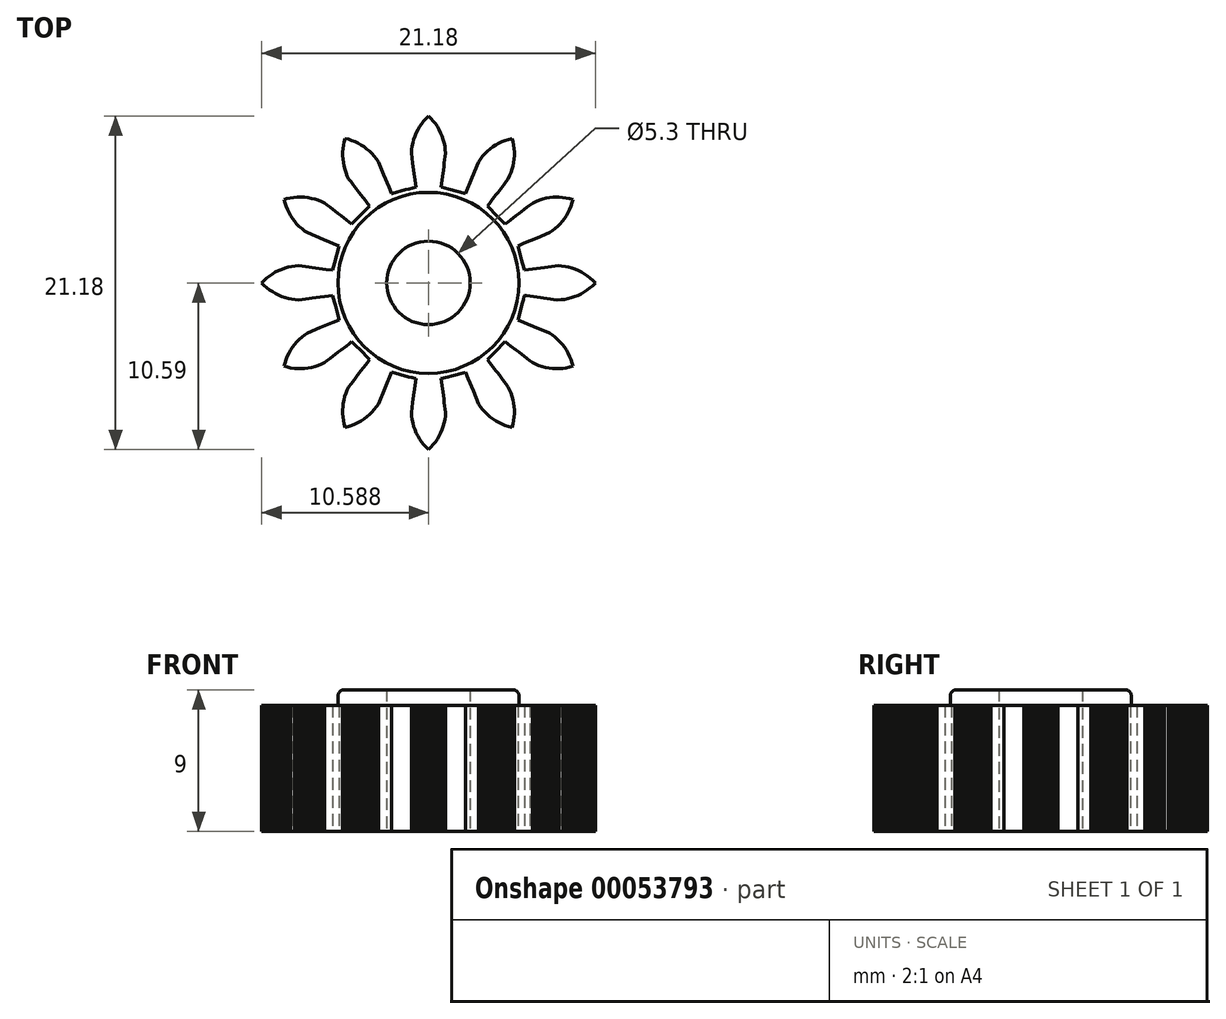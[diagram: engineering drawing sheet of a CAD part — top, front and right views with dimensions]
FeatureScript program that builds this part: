
annotation { "Feature Type Name" : "Feature", "Feature Type Description" : "" }
export const myFeature = defineFeature(function(context is Context, id is Id, definition is map)
    precondition{}
    {
        {
            var Q0;
            Q0=qCreatedBy(makeId("Top.planeOp"),FACE);
            var sketch = newSketch(context, id + "F0", { "sketchPlane" : qUnion([Q0])});
            skLineSegment(sketch, "E0", {"start": v(4.76, -0.8) * mm, "end": v(4.9, -0.82) * mm});
            skLineSegment(sketch, "E1", {"start": v(4.9, -0.82) * mm, "end": v(5.12, -0.85) * mm});
            skLineSegment(sketch, "E2", {"start": v(5.12, -0.85) * mm, "end": v(5.33, -0.88) * mm});
            skLineSegment(sketch, "E3", {"start": v(5.33, -0.88) * mm, "end": v(5.55, -0.9) * mm});
            skLineSegment(sketch, "E4", {"start": v(5.55, -0.9) * mm, "end": v(5.76, -0.93) * mm});
            skLineSegment(sketch, "E5", {"start": v(5.76, -0.93) * mm, "end": v(5.98, -0.96) * mm});
            skLineSegment(sketch, "E6", {"start": v(5.98, -0.96) * mm, "end": v(6.2, -1) * mm});
            skLineSegment(sketch, "E7", {"start": v(6.2, -1) * mm, "end": v(6.41, -1.02) * mm});
            skLineSegment(sketch, "E8", {"start": v(6.41, -1.02) * mm, "end": v(6.63, -1.05) * mm});
            skLineSegment(sketch, "E9", {"start": v(6.63, -1.05) * mm, "end": v(6.84, -1.08) * mm});
            skLineSegment(sketch, "E10", {"start": v(6.84, -1.08) * mm, "end": v(7.07, -1.07) * mm});
            skLineSegment(sketch, "E11", {"start": v(7.07, -1.07) * mm, "end": v(7.3, -1.05) * mm});
            skLineSegment(sketch, "E12", {"start": v(7.3, -1.05) * mm, "end": v(7.53, -1) * mm});
            skLineSegment(sketch, "E13", {"start": v(7.53, -1) * mm, "end": v(7.75, -0.95) * mm});
            skLineSegment(sketch, "E14", {"start": v(7.75, -0.95) * mm, "end": v(7.95, -0.88) * mm});
            skLineSegment(sketch, "E15", {"start": v(7.95, -0.88) * mm, "end": v(8.16, -0.8) * mm});
            skLineSegment(sketch, "E16", {"start": v(8.16, -0.8) * mm, "end": v(8.36, -0.7) * mm});
            skLineSegment(sketch, "E17", {"start": v(8.36, -0.7) * mm, "end": v(8.55, -0.59) * mm});
            skLineSegment(sketch, "E18", {"start": v(8.55, -0.59) * mm, "end": v(8.73, -0.47) * mm});
            skLineSegment(sketch, "E19", {"start": v(8.73, -0.47) * mm, "end": v(8.9, -0.33) * mm});
            skLineSegment(sketch, "E20", {"start": v(8.9, -0.33) * mm, "end": v(9.07, -0.19) * mm});
            skLineSegment(sketch, "E21", {"start": v(9.07, -0.19) * mm, "end": v(9.23, -0.03) * mm});
            skLineSegment(sketch, "E22", {"start": v(9.23, -0.03) * mm, "end": v(9.26, 0) * mm});
            skLineSegment(sketch, "E23", {"start": v(9.26, 0) * mm, "end": v(9.1, 0.16) * mm});
            skLineSegment(sketch, "E24", {"start": v(9.1, 0.16) * mm, "end": v(8.94, 0.3) * mm});
            skLineSegment(sketch, "E25", {"start": v(8.94, 0.3) * mm, "end": v(8.76, 0.44) * mm});
            skLineSegment(sketch, "E26", {"start": v(8.76, 0.44) * mm, "end": v(8.58, 0.57) * mm});
            skLineSegment(sketch, "E27", {"start": v(8.58, 0.57) * mm, "end": v(8.39, 0.68) * mm});
            skLineSegment(sketch, "E28", {"start": v(8.39, 0.68) * mm, "end": v(8.2, 0.78) * mm});
            skLineSegment(sketch, "E29", {"start": v(8.2, 0.78) * mm, "end": v(7.99, 0.86) * mm});
            skLineSegment(sketch, "E30", {"start": v(7.99, 0.86) * mm, "end": v(7.78, 0.94) * mm});
            skLineSegment(sketch, "E31", {"start": v(7.78, 0.94) * mm, "end": v(7.57, 1) * mm});
            skLineSegment(sketch, "E32", {"start": v(7.57, 1) * mm, "end": v(7.36, 1.04) * mm});
            skLineSegment(sketch, "E33", {"start": v(7.36, 1.04) * mm, "end": v(7.13, 1.07) * mm});
            skLineSegment(sketch, "E34", {"start": v(7.13, 1.07) * mm, "end": v(6.92, 1.09) * mm});
            skLineSegment(sketch, "E35", {"start": v(6.92, 1.09) * mm, "end": v(6.7, 1.06) * mm});
            skLineSegment(sketch, "E36", {"start": v(6.7, 1.06) * mm, "end": v(6.48, 1.03) * mm});
            skLineSegment(sketch, "E37", {"start": v(6.48, 1.03) * mm, "end": v(6.27, 1) * mm});
            skLineSegment(sketch, "E38", {"start": v(6.27, 1) * mm, "end": v(6.05, 0.97) * mm});
            skLineSegment(sketch, "E39", {"start": v(6.05, 0.97) * mm, "end": v(5.84, 0.94) * mm});
            skLineSegment(sketch, "E40", {"start": v(5.84, 0.94) * mm, "end": v(5.62, 0.92) * mm});
            skLineSegment(sketch, "E41", {"start": v(5.62, 0.92) * mm, "end": v(5.4, 0.89) * mm});
            skLineSegment(sketch, "E42", {"start": v(5.4, 0.89) * mm, "end": v(5.19, 0.86) * mm});
            skLineSegment(sketch, "E43", {"start": v(5.19, 0.86) * mm, "end": v(4.97, 0.83) * mm});
            skLineSegment(sketch, "E44", {"start": v(4.97, 0.83) * mm, "end": v(4.76, 0.8) * mm});
            skLineSegment(sketch, "E45", {"start": v(4.76, 0.8) * mm, "end": v(4.7, 1.02) * mm});
            skLineSegment(sketch, "E46", {"start": v(4.7, 1.02) * mm, "end": v(4.64, 1.24) * mm});
            skLineSegment(sketch, "E47", {"start": v(4.64, 1.24) * mm, "end": v(4.58, 1.45) * mm});
            skLineSegment(sketch, "E48", {"start": v(4.58, 1.45) * mm, "end": v(4.52, 1.67) * mm});
            skLineSegment(sketch, "E49", {"start": v(4.52, 1.67) * mm, "end": v(4.47, 1.89) * mm});
            skLineSegment(sketch, "E50", {"start": v(4.47, 1.89) * mm, "end": v(4.4, 2.1) * mm});
            skLineSegment(sketch, "E51", {"start": v(4.4, 2.1) * mm, "end": v(4.35, 2.32) * mm});
            skLineSegment(sketch, "E52", {"start": v(4.35, 2.32) * mm, "end": v(4.34, 2.35) * mm});
            skLineSegment(sketch, "E53", {"start": v(4.34, 2.35) * mm, "end": v(4.54, 2.43) * mm});
            skLineSegment(sketch, "E54", {"start": v(4.54, 2.43) * mm, "end": v(4.74, 2.52) * mm});
            skLineSegment(sketch, "E55", {"start": v(4.74, 2.52) * mm, "end": v(4.95, 2.6) * mm});
            skLineSegment(sketch, "E56", {"start": v(4.95, 2.6) * mm, "end": v(5.15, 2.68) * mm});
            skLineSegment(sketch, "E57", {"start": v(5.15, 2.68) * mm, "end": v(5.35, 2.77) * mm});
            skLineSegment(sketch, "E58", {"start": v(5.35, 2.77) * mm, "end": v(5.55, 2.85) * mm});
            skLineSegment(sketch, "E59", {"start": v(5.55, 2.85) * mm, "end": v(5.75, 2.93) * mm});
            skLineSegment(sketch, "E60", {"start": v(5.75, 2.93) * mm, "end": v(5.95, 3.02) * mm});
            skLineSegment(sketch, "E61", {"start": v(5.95, 3.02) * mm, "end": v(6.15, 3.1) * mm});
            skLineSegment(sketch, "E62", {"start": v(6.15, 3.1) * mm, "end": v(6.35, 3.18) * mm});
            skLineSegment(sketch, "E63", {"start": v(6.35, 3.18) * mm, "end": v(6.54, 3.31) * mm});
            skLineSegment(sketch, "E64", {"start": v(6.54, 3.31) * mm, "end": v(6.71, 3.44) * mm});
            skLineSegment(sketch, "E65", {"start": v(6.71, 3.44) * mm, "end": v(6.88, 3.6) * mm});
            skLineSegment(sketch, "E66", {"start": v(6.88, 3.6) * mm, "end": v(7.03, 3.75) * mm});
            skLineSegment(sketch, "E67", {"start": v(7.03, 3.75) * mm, "end": v(7.18, 3.92) * mm});
            skLineSegment(sketch, "E68", {"start": v(7.18, 3.92) * mm, "end": v(7.3, 4.1) * mm});
            skLineSegment(sketch, "E69", {"start": v(7.3, 4.1) * mm, "end": v(7.43, 4.28) * mm});
            skLineSegment(sketch, "E70", {"start": v(7.43, 4.28) * mm, "end": v(7.54, 4.47) * mm});
            skLineSegment(sketch, "E71", {"start": v(7.54, 4.47) * mm, "end": v(7.64, 4.67) * mm});
            skLineSegment(sketch, "E72", {"start": v(7.64, 4.67) * mm, "end": v(7.72, 4.87) * mm});
            skLineSegment(sketch, "E73", {"start": v(7.72, 4.87) * mm, "end": v(7.79, 5.09) * mm});
            skLineSegment(sketch, "E74", {"start": v(7.79, 5.09) * mm, "end": v(7.84, 5.3) * mm});
            skLineSegment(sketch, "E75", {"start": v(7.84, 5.3) * mm, "end": v(7.62, 5.36) * mm});
            skLineSegment(sketch, "E76", {"start": v(7.62, 5.36) * mm, "end": v(7.41, 5.4) * mm});
            skLineSegment(sketch, "E77", {"start": v(7.41, 5.4) * mm, "end": v(7.19, 5.43) * mm});
            skLineSegment(sketch, "E78", {"start": v(7.19, 5.43) * mm, "end": v(6.97, 5.45) * mm});
            skLineSegment(sketch, "E79", {"start": v(6.97, 5.45) * mm, "end": v(6.8, 5.45) * mm});
            skLineSegment(sketch, "E80", {"start": v(6.8, 5.45) * mm, "end": v(6.57, 5.44) * mm});
            skLineSegment(sketch, "E81", {"start": v(6.57, 5.44) * mm, "end": v(6.36, 5.42) * mm});
            skLineSegment(sketch, "E82", {"start": v(6.36, 5.42) * mm, "end": v(6.13, 5.38) * mm});
            skLineSegment(sketch, "E83", {"start": v(6.13, 5.38) * mm, "end": v(5.92, 5.33) * mm});
            skLineSegment(sketch, "E84", {"start": v(5.92, 5.33) * mm, "end": v(5.7, 5.26) * mm});
            skLineSegment(sketch, "E85", {"start": v(5.7, 5.26) * mm, "end": v(5.5, 5.18) * mm});
            skLineSegment(sketch, "E86", {"start": v(5.5, 5.18) * mm, "end": v(5.3, 5.08) * mm});
            skLineSegment(sketch, "E87", {"start": v(5.3, 5.08) * mm, "end": v(5.12, 4.95) * mm});
            skLineSegment(sketch, "E88", {"start": v(5.12, 4.95) * mm, "end": v(4.94, 4.81) * mm});
            skLineSegment(sketch, "E89", {"start": v(4.94, 4.81) * mm, "end": v(4.75, 4.67) * mm});
            skLineSegment(sketch, "E90", {"start": v(4.75, 4.67) * mm, "end": v(4.58, 4.53) * mm});
            skLineSegment(sketch, "E91", {"start": v(4.58, 4.53) * mm, "end": v(4.4, 4.4) * mm});
            skLineSegment(sketch, "E92", {"start": v(4.4, 4.4) * mm, "end": v(4.23, 4.27) * mm});
            skLineSegment(sketch, "E93", {"start": v(4.23, 4.27) * mm, "end": v(4.06, 4.14) * mm});
            skLineSegment(sketch, "E94", {"start": v(4.06, 4.14) * mm, "end": v(3.89, 4) * mm});
            skLineSegment(sketch, "E95", {"start": v(3.89, 4) * mm, "end": v(3.71, 3.87) * mm});
            skLineSegment(sketch, "E96", {"start": v(3.71, 3.87) * mm, "end": v(3.54, 3.74) * mm});
            skLineSegment(sketch, "E97", {"start": v(3.54, 3.74) * mm, "end": v(3.38, 3.9) * mm});
            skLineSegment(sketch, "E98", {"start": v(3.38, 3.9) * mm, "end": v(3.22, 4.06) * mm});
            skLineSegment(sketch, "E99", {"start": v(3.22, 4.06) * mm, "end": v(3.06, 4.22) * mm});
            skLineSegment(sketch, "E100", {"start": v(3.06, 4.22) * mm, "end": v(2.9, 4.38) * mm});
            skLineSegment(sketch, "E101", {"start": v(2.9, 4.38) * mm, "end": v(2.74, 4.53) * mm});
            skLineSegment(sketch, "E102", {"start": v(2.74, 4.53) * mm, "end": v(2.58, 4.7) * mm});
            skLineSegment(sketch, "E103", {"start": v(2.58, 4.7) * mm, "end": v(2.43, 4.85) * mm});
            skLineSegment(sketch, "E104", {"start": v(2.43, 4.85) * mm, "end": v(2.4, 4.87) * mm});
            skLineSegment(sketch, "E105", {"start": v(2.4, 4.87) * mm, "end": v(2.54, 5.04) * mm});
            skLineSegment(sketch, "E106", {"start": v(2.54, 5.04) * mm, "end": v(2.67, 5.22) * mm});
            skLineSegment(sketch, "E107", {"start": v(2.67, 5.22) * mm, "end": v(2.8, 5.4) * mm});
            skLineSegment(sketch, "E108", {"start": v(2.8, 5.4) * mm, "end": v(2.94, 5.56) * mm});
            skLineSegment(sketch, "E109", {"start": v(2.94, 5.56) * mm, "end": v(3.07, 5.74) * mm});
            skLineSegment(sketch, "E110", {"start": v(3.07, 5.74) * mm, "end": v(3.2, 5.9) * mm});
            skLineSegment(sketch, "E111", {"start": v(3.2, 5.9) * mm, "end": v(3.33, 6.08) * mm});
            skLineSegment(sketch, "E112", {"start": v(3.33, 6.08) * mm, "end": v(3.47, 6.25) * mm});
            skLineSegment(sketch, "E113", {"start": v(3.47, 6.25) * mm, "end": v(3.6, 6.43) * mm});
            skLineSegment(sketch, "E114", {"start": v(3.6, 6.43) * mm, "end": v(3.73, 6.6) * mm});
            skLineSegment(sketch, "E115", {"start": v(3.73, 6.6) * mm, "end": v(3.83, 6.8) * mm});
            skLineSegment(sketch, "E116", {"start": v(3.83, 6.8) * mm, "end": v(3.91, 7) * mm});
            skLineSegment(sketch, "E117", {"start": v(3.91, 7) * mm, "end": v(3.98, 7.22) * mm});
            skLineSegment(sketch, "E118", {"start": v(3.98, 7.22) * mm, "end": v(4.04, 7.43) * mm});
            skLineSegment(sketch, "E119", {"start": v(4.04, 7.43) * mm, "end": v(4.08, 7.65) * mm});
            skLineSegment(sketch, "E120", {"start": v(4.08, 7.65) * mm, "end": v(4.1, 7.86) * mm});
            skLineSegment(sketch, "E121", {"start": v(4.1, 7.86) * mm, "end": v(4.12, 8.09) * mm});
            skLineSegment(sketch, "E122", {"start": v(4.12, 8.09) * mm, "end": v(4.12, 8.3) * mm});
            skLineSegment(sketch, "E123", {"start": v(4.12, 8.3) * mm, "end": v(4.1, 8.53) * mm});
            skLineSegment(sketch, "E124", {"start": v(4.1, 8.53) * mm, "end": v(4.07, 8.74) * mm});
            skLineSegment(sketch, "E125", {"start": v(4.07, 8.74) * mm, "end": v(4.02, 8.96) * mm});
            skLineSegment(sketch, "E126", {"start": v(4.02, 8.96) * mm, "end": v(3.96, 9.17) * mm});
            skLineSegment(sketch, "E127", {"start": v(3.96, 9.17) * mm, "end": v(3.75, 9.12) * mm});
            skLineSegment(sketch, "E128", {"start": v(3.75, 9.12) * mm, "end": v(3.54, 9.05) * mm});
            skLineSegment(sketch, "E129", {"start": v(3.54, 9.05) * mm, "end": v(3.33, 8.96) * mm});
            skLineSegment(sketch, "E130", {"start": v(3.33, 8.96) * mm, "end": v(3.14, 8.87) * mm});
            skLineSegment(sketch, "E131", {"start": v(3.14, 8.87) * mm, "end": v(2.94, 8.76) * mm});
            skLineSegment(sketch, "E132", {"start": v(2.94, 8.76) * mm, "end": v(2.76, 8.64) * mm});
            skLineSegment(sketch, "E133", {"start": v(2.76, 8.64) * mm, "end": v(2.58, 8.5) * mm});
            skLineSegment(sketch, "E134", {"start": v(2.58, 8.5) * mm, "end": v(2.42, 8.36) * mm});
            skLineSegment(sketch, "E135", {"start": v(2.42, 8.36) * mm, "end": v(2.26, 8.2) * mm});
            skLineSegment(sketch, "E136", {"start": v(2.26, 8.2) * mm, "end": v(2.11, 8.04) * mm});
            skLineSegment(sketch, "E137", {"start": v(2.11, 8.04) * mm, "end": v(1.97, 7.86) * mm});
            skLineSegment(sketch, "E138", {"start": v(1.97, 7.86) * mm, "end": v(1.85, 7.69) * mm});
            skLineSegment(sketch, "E139", {"start": v(1.85, 7.69) * mm, "end": v(1.77, 7.48) * mm});
            skLineSegment(sketch, "E140", {"start": v(1.77, 7.48) * mm, "end": v(1.69, 7.28) * mm});
            skLineSegment(sketch, "E141", {"start": v(1.69, 7.28) * mm, "end": v(1.6, 7.08) * mm});
            skLineSegment(sketch, "E142", {"start": v(1.6, 7.08) * mm, "end": v(1.52, 6.88) * mm});
            skLineSegment(sketch, "E143", {"start": v(1.52, 6.88) * mm, "end": v(1.44, 6.68) * mm});
            skLineSegment(sketch, "E144", {"start": v(1.44, 6.68) * mm, "end": v(1.35, 6.48) * mm});
            skLineSegment(sketch, "E145", {"start": v(1.35, 6.48) * mm, "end": v(1.27, 6.28) * mm});
            skLineSegment(sketch, "E146", {"start": v(1.27, 6.28) * mm, "end": v(1.18, 6.08) * mm});
            skLineSegment(sketch, "E147", {"start": v(1.18, 6.08) * mm, "end": v(1.1, 5.87) * mm});
            skLineSegment(sketch, "E148", {"start": v(1.1, 5.87) * mm, "end": v(1.02, 5.67) * mm});
            skLineSegment(sketch, "E149", {"start": v(1.02, 5.67) * mm, "end": v(0.8, 5.73) * mm});
            skLineSegment(sketch, "E150", {"start": v(0.8, 5.73) * mm, "end": v(0.58, 5.8) * mm});
            skLineSegment(sketch, "E151", {"start": v(0.58, 5.8) * mm, "end": v(0.37, 5.85) * mm});
            skLineSegment(sketch, "E152", {"start": v(0.37, 5.85) * mm, "end": v(0.15, 5.9) * mm});
            skLineSegment(sketch, "E153", {"start": v(0.15, 5.9) * mm, "end": v(-0.07, 5.97) * mm});
            skLineSegment(sketch, "E154", {"start": v(-0.07, 5.97) * mm, "end": v(-0.29, 6.02) * mm});
            skLineSegment(sketch, "E155", {"start": v(-0.29, 6.02) * mm, "end": v(-0.5, 6.08) * mm});
            skLineSegment(sketch, "E156", {"start": v(-0.5, 6.08) * mm, "end": v(-0.53, 6.09) * mm});
            skLineSegment(sketch, "E157", {"start": v(-0.53, 6.09) * mm, "end": v(-0.5, 6.3) * mm});
            skLineSegment(sketch, "E158", {"start": v(-0.5, 6.3) * mm, "end": v(-0.47, 6.52) * mm});
            skLineSegment(sketch, "E159", {"start": v(-0.47, 6.52) * mm, "end": v(-0.44, 6.74) * mm});
            skLineSegment(sketch, "E160", {"start": v(-0.44, 6.74) * mm, "end": v(-0.42, 6.95) * mm});
            skLineSegment(sketch, "E161", {"start": v(-0.42, 6.95) * mm, "end": v(-0.39, 7.17) * mm});
            skLineSegment(sketch, "E162", {"start": v(-0.39, 7.17) * mm, "end": v(-0.36, 7.38) * mm});
            skLineSegment(sketch, "E163", {"start": v(-0.36, 7.38) * mm, "end": v(-0.33, 7.6) * mm});
            skLineSegment(sketch, "E164", {"start": v(-0.33, 7.6) * mm, "end": v(-0.3, 7.82) * mm});
            skLineSegment(sketch, "E165", {"start": v(-0.3, 7.82) * mm, "end": v(-0.27, 8.03) * mm});
            skLineSegment(sketch, "E166", {"start": v(-0.27, 8.03) * mm, "end": v(-0.25, 8.25) * mm});
            skLineSegment(sketch, "E167", {"start": v(-0.25, 8.25) * mm, "end": v(-0.26, 8.47) * mm});
            skLineSegment(sketch, "E168", {"start": v(-0.26, 8.47) * mm, "end": v(-0.3, 8.69) * mm});
            skLineSegment(sketch, "E169", {"start": v(-0.3, 8.69) * mm, "end": v(-0.34, 8.9) * mm});
            skLineSegment(sketch, "E170", {"start": v(-0.34, 8.9) * mm, "end": v(-0.4, 9.12) * mm});
            skLineSegment(sketch, "E171", {"start": v(-0.4, 9.12) * mm, "end": v(-0.47, 9.33) * mm});
            skLineSegment(sketch, "E172", {"start": v(-0.47, 9.33) * mm, "end": v(-0.55, 9.53) * mm});
            skLineSegment(sketch, "E173", {"start": v(-0.55, 9.53) * mm, "end": v(-0.66, 9.73) * mm});
            skLineSegment(sketch, "E174", {"start": v(-0.66, 9.73) * mm, "end": v(-0.77, 9.92) * mm});
            skLineSegment(sketch, "E175", {"start": v(-0.77, 9.92) * mm, "end": v(-0.9, 10.1) * mm});
            skLineSegment(sketch, "E176", {"start": v(-0.9, 10.1) * mm, "end": v(-1.03, 10.27) * mm});
            skLineSegment(sketch, "E177", {"start": v(-1.03, 10.27) * mm, "end": v(-1.18, 10.44) * mm});
            skLineSegment(sketch, "E178", {"start": v(-1.18, 10.44) * mm, "end": v(-1.33, 10.6) * mm});
            skLineSegment(sketch, "E179", {"start": v(-1.33, 10.6) * mm, "end": v(-1.5, 10.43) * mm});
            skLineSegment(sketch, "E180", {"start": v(-1.5, 10.43) * mm, "end": v(-1.64, 10.27) * mm});
            skLineSegment(sketch, "E181", {"start": v(-1.64, 10.27) * mm, "end": v(-1.78, 10.1) * mm});
            skLineSegment(sketch, "E182", {"start": v(-1.78, 10.1) * mm, "end": v(-1.9, 9.92) * mm});
            skLineSegment(sketch, "E183", {"start": v(-1.9, 9.92) * mm, "end": v(-2.01, 9.72) * mm});
            skLineSegment(sketch, "E184", {"start": v(-2.01, 9.72) * mm, "end": v(-2.1, 9.53) * mm});
            skLineSegment(sketch, "E185", {"start": v(-2.1, 9.53) * mm, "end": v(-2.2, 9.32) * mm});
            skLineSegment(sketch, "E186", {"start": v(-2.2, 9.32) * mm, "end": v(-2.27, 9.12) * mm});
            skLineSegment(sketch, "E187", {"start": v(-2.27, 9.12) * mm, "end": v(-2.33, 8.9) * mm});
            skLineSegment(sketch, "E188", {"start": v(-2.33, 8.9) * mm, "end": v(-2.37, 8.69) * mm});
            skLineSegment(sketch, "E189", {"start": v(-2.37, 8.69) * mm, "end": v(-2.4, 8.46) * mm});
            skLineSegment(sketch, "E190", {"start": v(-2.4, 8.46) * mm, "end": v(-2.42, 8.25) * mm});
            skLineSegment(sketch, "E191", {"start": v(-2.42, 8.25) * mm, "end": v(-2.39, 8.03) * mm});
            skLineSegment(sketch, "E192", {"start": v(-2.39, 8.03) * mm, "end": v(-2.36, 7.82) * mm});
            skLineSegment(sketch, "E193", {"start": v(-2.36, 7.82) * mm, "end": v(-2.33, 7.6) * mm});
            skLineSegment(sketch, "E194", {"start": v(-2.33, 7.6) * mm, "end": v(-2.3, 7.38) * mm});
            skLineSegment(sketch, "E195", {"start": v(-2.3, 7.38) * mm, "end": v(-2.28, 7.17) * mm});
            skLineSegment(sketch, "E196", {"start": v(-2.28, 7.17) * mm, "end": v(-2.25, 6.95) * mm});
            skLineSegment(sketch, "E197", {"start": v(-2.25, 6.95) * mm, "end": v(-2.22, 6.74) * mm});
            skLineSegment(sketch, "E198", {"start": v(-2.22, 6.74) * mm, "end": v(-2.2, 6.52) * mm});
            skLineSegment(sketch, "E199", {"start": v(-2.2, 6.52) * mm, "end": v(-2.16, 6.3) * mm});
            skLineSegment(sketch, "E200", {"start": v(-2.16, 6.3) * mm, "end": v(-2.13, 6.09) * mm});
            skLineSegment(sketch, "E201", {"start": v(-2.13, 6.09) * mm, "end": v(-2.35, 6.03) * mm});
            skLineSegment(sketch, "E202", {"start": v(-2.35, 6.03) * mm, "end": v(-2.57, 5.97) * mm});
            skLineSegment(sketch, "E203", {"start": v(-2.57, 5.97) * mm, "end": v(-2.79, 5.91) * mm});
            skLineSegment(sketch, "E204", {"start": v(-2.79, 5.91) * mm, "end": v(-3, 5.86) * mm});
            skLineSegment(sketch, "E205", {"start": v(-3, 5.86) * mm, "end": v(-3.22, 5.8) * mm});
            skLineSegment(sketch, "E206", {"start": v(-3.22, 5.8) * mm, "end": v(-3.44, 5.74) * mm});
            skLineSegment(sketch, "E207", {"start": v(-3.44, 5.74) * mm, "end": v(-3.66, 5.68) * mm});
            skLineSegment(sketch, "E208", {"start": v(-3.66, 5.68) * mm, "end": v(-3.68, 5.67) * mm});
            skLineSegment(sketch, "E209", {"start": v(-3.68, 5.67) * mm, "end": v(-3.77, 5.87) * mm});
            skLineSegment(sketch, "E210", {"start": v(-3.77, 5.87) * mm, "end": v(-3.85, 6.08) * mm});
            skLineSegment(sketch, "E211", {"start": v(-3.85, 6.08) * mm, "end": v(-3.93, 6.28) * mm});
            skLineSegment(sketch, "E212", {"start": v(-3.93, 6.28) * mm, "end": v(-4.02, 6.48) * mm});
            skLineSegment(sketch, "E213", {"start": v(-4.02, 6.48) * mm, "end": v(-4.1, 6.68) * mm});
            skLineSegment(sketch, "E214", {"start": v(-4.1, 6.68) * mm, "end": v(-4.18, 6.88) * mm});
            skLineSegment(sketch, "E215", {"start": v(-4.18, 6.88) * mm, "end": v(-4.27, 7.08) * mm});
            skLineSegment(sketch, "E216", {"start": v(-4.27, 7.08) * mm, "end": v(-4.35, 7.28) * mm});
            skLineSegment(sketch, "E217", {"start": v(-4.35, 7.28) * mm, "end": v(-4.43, 7.48) * mm});
            skLineSegment(sketch, "E218", {"start": v(-4.43, 7.48) * mm, "end": v(-4.52, 7.69) * mm});
            skLineSegment(sketch, "E219", {"start": v(-4.52, 7.69) * mm, "end": v(-4.64, 7.87) * mm});
            skLineSegment(sketch, "E220", {"start": v(-4.64, 7.87) * mm, "end": v(-4.77, 8.04) * mm});
            skLineSegment(sketch, "E221", {"start": v(-4.77, 8.04) * mm, "end": v(-4.93, 8.21) * mm});
            skLineSegment(sketch, "E222", {"start": v(-4.93, 8.21) * mm, "end": v(-5.08, 8.36) * mm});
            skLineSegment(sketch, "E223", {"start": v(-5.08, 8.36) * mm, "end": v(-5.25, 8.5) * mm});
            skLineSegment(sketch, "E224", {"start": v(-5.25, 8.5) * mm, "end": v(-5.42, 8.64) * mm});
            skLineSegment(sketch, "E225", {"start": v(-5.42, 8.64) * mm, "end": v(-5.61, 8.76) * mm});
            skLineSegment(sketch, "E226", {"start": v(-5.61, 8.76) * mm, "end": v(-5.8, 8.87) * mm});
            skLineSegment(sketch, "E227", {"start": v(-5.8, 8.87) * mm, "end": v(-6, 8.97) * mm});
            skLineSegment(sketch, "E228", {"start": v(-6, 8.97) * mm, "end": v(-6.2, 9.05) * mm});
            skLineSegment(sketch, "E229", {"start": v(-6.2, 9.05) * mm, "end": v(-6.42, 9.12) * mm});
            skLineSegment(sketch, "E230", {"start": v(-6.42, 9.12) * mm, "end": v(-6.63, 9.17) * mm});
            skLineSegment(sketch, "E231", {"start": v(-6.63, 9.17) * mm, "end": v(-6.69, 8.96) * mm});
            skLineSegment(sketch, "E232", {"start": v(-6.69, 8.96) * mm, "end": v(-6.73, 8.74) * mm});
            skLineSegment(sketch, "E233", {"start": v(-6.73, 8.74) * mm, "end": v(-6.76, 8.52) * mm});
            skLineSegment(sketch, "E234", {"start": v(-6.76, 8.52) * mm, "end": v(-6.78, 8.3) * mm});
            skLineSegment(sketch, "E235", {"start": v(-6.78, 8.3) * mm, "end": v(-6.78, 8.08) * mm});
            skLineSegment(sketch, "E236", {"start": v(-6.78, 8.08) * mm, "end": v(-6.77, 7.86) * mm});
            skLineSegment(sketch, "E237", {"start": v(-6.77, 7.86) * mm, "end": v(-6.74, 7.64) * mm});
            skLineSegment(sketch, "E238", {"start": v(-6.74, 7.64) * mm, "end": v(-6.7, 7.43) * mm});
            skLineSegment(sketch, "E239", {"start": v(-6.7, 7.43) * mm, "end": v(-6.64, 7.2) * mm});
            skLineSegment(sketch, "E240", {"start": v(-6.64, 7.2) * mm, "end": v(-6.58, 7) * mm});
            skLineSegment(sketch, "E241", {"start": v(-6.58, 7) * mm, "end": v(-6.49, 6.8) * mm});
            skLineSegment(sketch, "E242", {"start": v(-6.49, 6.8) * mm, "end": v(-6.4, 6.6) * mm});
            skLineSegment(sketch, "E243", {"start": v(-6.4, 6.6) * mm, "end": v(-6.26, 6.43) * mm});
            skLineSegment(sketch, "E244", {"start": v(-6.26, 6.43) * mm, "end": v(-6.13, 6.25) * mm});
            skLineSegment(sketch, "E245", {"start": v(-6.13, 6.25) * mm, "end": v(-6, 6.08) * mm});
            skLineSegment(sketch, "E246", {"start": v(-6, 6.08) * mm, "end": v(-5.87, 5.9) * mm});
            skLineSegment(sketch, "E247", {"start": v(-5.87, 5.9) * mm, "end": v(-5.73, 5.74) * mm});
            skLineSegment(sketch, "E248", {"start": v(-5.73, 5.74) * mm, "end": v(-5.6, 5.56) * mm});
            skLineSegment(sketch, "E249", {"start": v(-5.6, 5.56) * mm, "end": v(-5.47, 5.4) * mm});
            skLineSegment(sketch, "E250", {"start": v(-5.47, 5.4) * mm, "end": v(-5.34, 5.22) * mm});
            skLineSegment(sketch, "E251", {"start": v(-5.34, 5.22) * mm, "end": v(-5.2, 5.04) * mm});
            skLineSegment(sketch, "E252", {"start": v(-5.2, 5.04) * mm, "end": v(-5.07, 4.87) * mm});
            skLineSegment(sketch, "E253", {"start": v(-5.07, 4.87) * mm, "end": v(-5.23, 4.71) * mm});
            skLineSegment(sketch, "E254", {"start": v(-5.23, 4.71) * mm, "end": v(-5.39, 4.55) * mm});
            skLineSegment(sketch, "E255", {"start": v(-5.39, 4.55) * mm, "end": v(-5.55, 4.4) * mm});
            skLineSegment(sketch, "E256", {"start": v(-5.55, 4.4) * mm, "end": v(-5.7, 4.23) * mm});
            skLineSegment(sketch, "E257", {"start": v(-5.7, 4.23) * mm, "end": v(-5.87, 4.08) * mm});
            skLineSegment(sketch, "E258", {"start": v(-5.87, 4.08) * mm, "end": v(-6.03, 3.92) * mm});
            skLineSegment(sketch, "E259", {"start": v(-6.03, 3.92) * mm, "end": v(-6.19, 3.76) * mm});
            skLineSegment(sketch, "E260", {"start": v(-6.19, 3.76) * mm, "end": v(-6.2, 3.74) * mm});
            skLineSegment(sketch, "E261", {"start": v(-6.2, 3.74) * mm, "end": v(-6.38, 3.87) * mm});
            skLineSegment(sketch, "E262", {"start": v(-6.38, 3.87) * mm, "end": v(-6.55, 4) * mm});
            skLineSegment(sketch, "E263", {"start": v(-6.55, 4) * mm, "end": v(-6.72, 4.14) * mm});
            skLineSegment(sketch, "E264", {"start": v(-6.72, 4.14) * mm, "end": v(-6.9, 4.27) * mm});
            skLineSegment(sketch, "E265", {"start": v(-6.9, 4.27) * mm, "end": v(-7.07, 4.4) * mm});
            skLineSegment(sketch, "E266", {"start": v(-7.07, 4.4) * mm, "end": v(-7.24, 4.53) * mm});
            skLineSegment(sketch, "E267", {"start": v(-7.24, 4.53) * mm, "end": v(-7.41, 4.67) * mm});
            skLineSegment(sketch, "E268", {"start": v(-7.41, 4.67) * mm, "end": v(-7.59, 4.8) * mm});
            skLineSegment(sketch, "E269", {"start": v(-7.59, 4.8) * mm, "end": v(-7.76, 4.93) * mm});
            skLineSegment(sketch, "E270", {"start": v(-7.76, 4.93) * mm, "end": v(-7.93, 5.06) * mm});
            skLineSegment(sketch, "E271", {"start": v(-7.93, 5.06) * mm, "end": v(-8.13, 5.16) * mm});
            skLineSegment(sketch, "E272", {"start": v(-8.13, 5.16) * mm, "end": v(-8.33, 5.24) * mm});
            skLineSegment(sketch, "E273", {"start": v(-8.33, 5.24) * mm, "end": v(-8.55, 5.31) * mm});
            skLineSegment(sketch, "E274", {"start": v(-8.55, 5.31) * mm, "end": v(-8.76, 5.37) * mm});
            skLineSegment(sketch, "E275", {"start": v(-8.76, 5.37) * mm, "end": v(-8.98, 5.41) * mm});
            skLineSegment(sketch, "E276", {"start": v(-8.98, 5.41) * mm, "end": v(-9.2, 5.44) * mm});
            skLineSegment(sketch, "E277", {"start": v(-9.2, 5.44) * mm, "end": v(-9.42, 5.45) * mm});
            skLineSegment(sketch, "E278", {"start": v(-9.42, 5.45) * mm, "end": v(-9.46, 5.45) * mm});
            skLineSegment(sketch, "E279", {"start": v(-9.46, 5.45) * mm, "end": v(-9.68, 5.44) * mm});
            skLineSegment(sketch, "E280", {"start": v(-9.68, 5.44) * mm, "end": v(-9.9, 5.43) * mm});
            skLineSegment(sketch, "E281", {"start": v(-9.9, 5.43) * mm, "end": v(-10.12, 5.4) * mm});
            skLineSegment(sketch, "E282", {"start": v(-10.12, 5.4) * mm, "end": v(-10.33, 5.34) * mm});
            skLineSegment(sketch, "E283", {"start": v(-10.33, 5.34) * mm, "end": v(-10.5, 5.3) * mm});
            skLineSegment(sketch, "E284", {"start": v(-10.5, 5.3) * mm, "end": v(-10.45, 5.08) * mm});
            skLineSegment(sketch, "E285", {"start": v(-10.45, 5.08) * mm, "end": v(-10.38, 4.87) * mm});
            skLineSegment(sketch, "E286", {"start": v(-10.38, 4.87) * mm, "end": v(-10.3, 4.66) * mm});
            skLineSegment(sketch, "E287", {"start": v(-10.3, 4.66) * mm, "end": v(-10.2, 4.47) * mm});
            skLineSegment(sketch, "E288", {"start": v(-10.2, 4.47) * mm, "end": v(-10.1, 4.27) * mm});
            skLineSegment(sketch, "E289", {"start": v(-10.1, 4.27) * mm, "end": v(-9.97, 4.1) * mm});
            skLineSegment(sketch, "E290", {"start": v(-9.97, 4.1) * mm, "end": v(-9.84, 3.91) * mm});
            skLineSegment(sketch, "E291", {"start": v(-9.84, 3.91) * mm, "end": v(-9.7, 3.75) * mm});
            skLineSegment(sketch, "E292", {"start": v(-9.7, 3.75) * mm, "end": v(-9.54, 3.59) * mm});
            skLineSegment(sketch, "E293", {"start": v(-9.54, 3.59) * mm, "end": v(-9.38, 3.44) * mm});
            skLineSegment(sketch, "E294", {"start": v(-9.38, 3.44) * mm, "end": v(-9.2, 3.3) * mm});
            skLineSegment(sketch, "E295", {"start": v(-9.2, 3.3) * mm, "end": v(-9.02, 3.18) * mm});
            skLineSegment(sketch, "E296", {"start": v(-9.02, 3.18) * mm, "end": v(-8.82, 3.1) * mm});
            skLineSegment(sketch, "E297", {"start": v(-8.82, 3.1) * mm, "end": v(-8.61, 3.02) * mm});
            skLineSegment(sketch, "E298", {"start": v(-8.61, 3.02) * mm, "end": v(-8.41, 2.93) * mm});
            skLineSegment(sketch, "E299", {"start": v(-8.41, 2.93) * mm, "end": v(-8.21, 2.85) * mm});
            skLineSegment(sketch, "E300", {"start": v(-8.21, 2.85) * mm, "end": v(-8.01, 2.77) * mm});
            skLineSegment(sketch, "E301", {"start": v(-8.01, 2.77) * mm, "end": v(-7.81, 2.68) * mm});
            skLineSegment(sketch, "E302", {"start": v(-7.81, 2.68) * mm, "end": v(-7.6, 2.6) * mm});
            skLineSegment(sketch, "E303", {"start": v(-7.6, 2.6) * mm, "end": v(-7.4, 2.52) * mm});
            skLineSegment(sketch, "E304", {"start": v(-7.4, 2.52) * mm, "end": v(-7.2, 2.43) * mm});
            skLineSegment(sketch, "E305", {"start": v(-7.2, 2.43) * mm, "end": v(-7, 2.35) * mm});
            skLineSegment(sketch, "E306", {"start": v(-7, 2.35) * mm, "end": v(-7.06, 2.13) * mm});
            skLineSegment(sketch, "E307", {"start": v(-7.06, 2.13) * mm, "end": v(-7.12, 1.91) * mm});
            skLineSegment(sketch, "E308", {"start": v(-7.12, 1.91) * mm, "end": v(-7.18, 1.7) * mm});
            skLineSegment(sketch, "E309", {"start": v(-7.18, 1.7) * mm, "end": v(-7.24, 1.48) * mm});
            skLineSegment(sketch, "E310", {"start": v(-7.24, 1.48) * mm, "end": v(-7.3, 1.26) * mm});
            skLineSegment(sketch, "E311", {"start": v(-7.3, 1.26) * mm, "end": v(-7.36, 1.04) * mm});
            skLineSegment(sketch, "E312", {"start": v(-7.36, 1.04) * mm, "end": v(-7.41, 0.83) * mm});
            skLineSegment(sketch, "E313", {"start": v(-7.41, 0.83) * mm, "end": v(-7.42, 0.8) * mm});
            skLineSegment(sketch, "E314", {"start": v(-7.42, 0.8) * mm, "end": v(-7.64, 0.83) * mm});
            skLineSegment(sketch, "E315", {"start": v(-7.64, 0.83) * mm, "end": v(-7.85, 0.86) * mm});
            skLineSegment(sketch, "E316", {"start": v(-7.85, 0.86) * mm, "end": v(-8.07, 0.89) * mm});
            skLineSegment(sketch, "E317", {"start": v(-8.07, 0.89) * mm, "end": v(-8.28, 0.92) * mm});
            skLineSegment(sketch, "E318", {"start": v(-8.28, 0.92) * mm, "end": v(-8.5, 0.94) * mm});
            skLineSegment(sketch, "E319", {"start": v(-8.5, 0.94) * mm, "end": v(-8.72, 0.97) * mm});
            skLineSegment(sketch, "E320", {"start": v(-8.72, 0.97) * mm, "end": v(-8.93, 1) * mm});
            skLineSegment(sketch, "E321", {"start": v(-8.93, 1) * mm, "end": v(-9.15, 1.03) * mm});
            skLineSegment(sketch, "E322", {"start": v(-9.15, 1.03) * mm, "end": v(-9.36, 1.06) * mm});
            skLineSegment(sketch, "E323", {"start": v(-9.36, 1.06) * mm, "end": v(-9.58, 1.09) * mm});
            skLineSegment(sketch, "E324", {"start": v(-9.58, 1.09) * mm, "end": v(-9.8, 1.07) * mm});
            skLineSegment(sketch, "E325", {"start": v(-9.8, 1.07) * mm, "end": v(-10.02, 1.04) * mm});
            skLineSegment(sketch, "E326", {"start": v(-10.02, 1.04) * mm, "end": v(-10.24, 1) * mm});
            skLineSegment(sketch, "E327", {"start": v(-10.24, 1) * mm, "end": v(-10.45, 0.94) * mm});
            skLineSegment(sketch, "E328", {"start": v(-10.45, 0.94) * mm, "end": v(-10.66, 0.86) * mm});
            skLineSegment(sketch, "E329", {"start": v(-10.66, 0.86) * mm, "end": v(-10.86, 0.78) * mm});
            skLineSegment(sketch, "E330", {"start": v(-10.86, 0.78) * mm, "end": v(-11.06, 0.68) * mm});
            skLineSegment(sketch, "E331", {"start": v(-11.06, 0.68) * mm, "end": v(-11.25, 0.57) * mm});
            skLineSegment(sketch, "E332", {"start": v(-11.25, 0.57) * mm, "end": v(-11.43, 0.44) * mm});
            skLineSegment(sketch, "E333", {"start": v(-11.43, 0.44) * mm, "end": v(-11.6, 0.3) * mm});
            skLineSegment(sketch, "E334", {"start": v(-11.6, 0.3) * mm, "end": v(-11.77, 0.15) * mm});
            skLineSegment(sketch, "E335", {"start": v(-11.77, 0.15) * mm, "end": v(-11.92, 0) * mm});
            skLineSegment(sketch, "E336", {"start": v(-11.92, 0) * mm, "end": v(-11.77, -0.16) * mm});
            skLineSegment(sketch, "E337", {"start": v(-11.77, -0.16) * mm, "end": v(-11.6, -0.3) * mm});
            skLineSegment(sketch, "E338", {"start": v(-11.6, -0.3) * mm, "end": v(-11.43, -0.44) * mm});
            skLineSegment(sketch, "E339", {"start": v(-11.43, -0.44) * mm, "end": v(-11.25, -0.57) * mm});
            skLineSegment(sketch, "E340", {"start": v(-11.25, -0.57) * mm, "end": v(-11.05, -0.68) * mm});
            skLineSegment(sketch, "E341", {"start": v(-11.05, -0.68) * mm, "end": v(-10.86, -0.78) * mm});
            skLineSegment(sketch, "E342", {"start": v(-10.86, -0.78) * mm, "end": v(-10.65, -0.86) * mm});
            skLineSegment(sketch, "E343", {"start": v(-10.65, -0.86) * mm, "end": v(-10.45, -0.94) * mm});
            skLineSegment(sketch, "E344", {"start": v(-10.45, -0.94) * mm, "end": v(-10.23, -1) * mm});
            skLineSegment(sketch, "E345", {"start": v(-10.23, -1) * mm, "end": v(-10.02, -1.04) * mm});
            skLineSegment(sketch, "E346", {"start": v(-10.02, -1.04) * mm, "end": v(-9.8, -1.07) * mm});
            skLineSegment(sketch, "E347", {"start": v(-9.8, -1.07) * mm, "end": v(-9.58, -1.09) * mm});
            skLineSegment(sketch, "E348", {"start": v(-9.58, -1.09) * mm, "end": v(-9.36, -1.06) * mm});
            skLineSegment(sketch, "E349", {"start": v(-9.36, -1.06) * mm, "end": v(-9.15, -1.03) * mm});
            skLineSegment(sketch, "E350", {"start": v(-9.15, -1.03) * mm, "end": v(-8.93, -1) * mm});
            skLineSegment(sketch, "E351", {"start": v(-8.93, -1) * mm, "end": v(-8.72, -0.97) * mm});
            skLineSegment(sketch, "E352", {"start": v(-8.72, -0.97) * mm, "end": v(-8.5, -0.94) * mm});
            skLineSegment(sketch, "E353", {"start": v(-8.5, -0.94) * mm, "end": v(-8.28, -0.92) * mm});
            skLineSegment(sketch, "E354", {"start": v(-8.28, -0.92) * mm, "end": v(-8.07, -0.89) * mm});
            skLineSegment(sketch, "E355", {"start": v(-8.07, -0.89) * mm, "end": v(-7.85, -0.86) * mm});
            skLineSegment(sketch, "E356", {"start": v(-7.85, -0.86) * mm, "end": v(-7.64, -0.83) * mm});
            skLineSegment(sketch, "E357", {"start": v(-7.64, -0.83) * mm, "end": v(-7.42, -0.8) * mm});
            skLineSegment(sketch, "E358", {"start": v(-7.42, -0.8) * mm, "end": v(-7.36, -1.02) * mm});
            skLineSegment(sketch, "E359", {"start": v(-7.36, -1.02) * mm, "end": v(-7.3, -1.24) * mm});
            skLineSegment(sketch, "E360", {"start": v(-7.3, -1.24) * mm, "end": v(-7.25, -1.45) * mm});
            skLineSegment(sketch, "E361", {"start": v(-7.25, -1.45) * mm, "end": v(-7.19, -1.67) * mm});
            skLineSegment(sketch, "E362", {"start": v(-7.19, -1.67) * mm, "end": v(-7.13, -1.89) * mm});
            skLineSegment(sketch, "E363", {"start": v(-7.13, -1.89) * mm, "end": v(-7.07, -2.1) * mm});
            skLineSegment(sketch, "E364", {"start": v(-7.07, -2.1) * mm, "end": v(-7.01, -2.32) * mm});
            skLineSegment(sketch, "E365", {"start": v(-7.01, -2.32) * mm, "end": v(-7, -2.35) * mm});
            skLineSegment(sketch, "E366", {"start": v(-7, -2.35) * mm, "end": v(-7.2, -2.43) * mm});
            skLineSegment(sketch, "E367", {"start": v(-7.2, -2.43) * mm, "end": v(-7.4, -2.52) * mm});
            skLineSegment(sketch, "E368", {"start": v(-7.4, -2.52) * mm, "end": v(-7.6, -2.6) * mm});
            skLineSegment(sketch, "E369", {"start": v(-7.6, -2.6) * mm, "end": v(-7.81, -2.68) * mm});
            skLineSegment(sketch, "E370", {"start": v(-7.81, -2.68) * mm, "end": v(-8.01, -2.77) * mm});
            skLineSegment(sketch, "E371", {"start": v(-8.01, -2.77) * mm, "end": v(-8.21, -2.85) * mm});
            skLineSegment(sketch, "E372", {"start": v(-8.21, -2.85) * mm, "end": v(-8.41, -2.93) * mm});
            skLineSegment(sketch, "E373", {"start": v(-8.41, -2.93) * mm, "end": v(-8.61, -3.02) * mm});
            skLineSegment(sketch, "E374", {"start": v(-8.61, -3.02) * mm, "end": v(-8.82, -3.1) * mm});
            skLineSegment(sketch, "E375", {"start": v(-8.82, -3.1) * mm, "end": v(-9.02, -3.18) * mm});
            skLineSegment(sketch, "E376", {"start": v(-9.02, -3.18) * mm, "end": v(-9.2, -3.31) * mm});
            skLineSegment(sketch, "E377", {"start": v(-9.2, -3.31) * mm, "end": v(-9.38, -3.44) * mm});
            skLineSegment(sketch, "E378", {"start": v(-9.38, -3.44) * mm, "end": v(-9.54, -3.6) * mm});
            skLineSegment(sketch, "E379", {"start": v(-9.54, -3.6) * mm, "end": v(-9.7, -3.75) * mm});
            skLineSegment(sketch, "E380", {"start": v(-9.7, -3.75) * mm, "end": v(-9.84, -3.92) * mm});
            skLineSegment(sketch, "E381", {"start": v(-9.84, -3.92) * mm, "end": v(-9.97, -4.1) * mm});
            skLineSegment(sketch, "E382", {"start": v(-9.97, -4.1) * mm, "end": v(-10.1, -4.28) * mm});
            skLineSegment(sketch, "E383", {"start": v(-10.1, -4.28) * mm, "end": v(-10.2, -4.47) * mm});
            skLineSegment(sketch, "E384", {"start": v(-10.2, -4.47) * mm, "end": v(-10.3, -4.67) * mm});
            skLineSegment(sketch, "E385", {"start": v(-10.3, -4.67) * mm, "end": v(-10.38, -4.87) * mm});
            skLineSegment(sketch, "E386", {"start": v(-10.38, -4.87) * mm, "end": v(-10.45, -5.09) * mm});
            skLineSegment(sketch, "E387", {"start": v(-10.45, -5.09) * mm, "end": v(-10.5, -5.3) * mm});
            skLineSegment(sketch, "E388", {"start": v(-10.5, -5.3) * mm, "end": v(-10.29, -5.36) * mm});
            skLineSegment(sketch, "E389", {"start": v(-10.29, -5.36) * mm, "end": v(-10.08, -5.4) * mm});
            skLineSegment(sketch, "E390", {"start": v(-10.08, -5.4) * mm, "end": v(-9.85, -5.43) * mm});
            skLineSegment(sketch, "E391", {"start": v(-9.85, -5.43) * mm, "end": v(-9.64, -5.45) * mm});
            skLineSegment(sketch, "E392", {"start": v(-9.64, -5.45) * mm, "end": v(-9.41, -5.45) * mm});
            skLineSegment(sketch, "E393", {"start": v(-9.41, -5.45) * mm, "end": v(-9.2, -5.44) * mm});
            skLineSegment(sketch, "E394", {"start": v(-9.2, -5.44) * mm, "end": v(-8.97, -5.4) * mm});
            skLineSegment(sketch, "E395", {"start": v(-8.97, -5.4) * mm, "end": v(-8.76, -5.37) * mm});
            skLineSegment(sketch, "E396", {"start": v(-8.76, -5.37) * mm, "end": v(-8.54, -5.31) * mm});
            skLineSegment(sketch, "E397", {"start": v(-8.54, -5.31) * mm, "end": v(-8.33, -5.24) * mm});
            skLineSegment(sketch, "E398", {"start": v(-8.33, -5.24) * mm, "end": v(-8.13, -5.16) * mm});
            skLineSegment(sketch, "E399", {"start": v(-8.13, -5.16) * mm, "end": v(-7.93, -5.06) * mm});
            skLineSegment(sketch, "E400", {"start": v(-7.93, -5.06) * mm, "end": v(-7.76, -4.93) * mm});
            skLineSegment(sketch, "E401", {"start": v(-7.76, -4.93) * mm, "end": v(-7.59, -4.8) * mm});
            skLineSegment(sketch, "E402", {"start": v(-7.59, -4.8) * mm, "end": v(-7.41, -4.67) * mm});
            skLineSegment(sketch, "E403", {"start": v(-7.41, -4.67) * mm, "end": v(-7.24, -4.53) * mm});
            skLineSegment(sketch, "E404", {"start": v(-7.24, -4.53) * mm, "end": v(-7.07, -4.4) * mm});
            skLineSegment(sketch, "E405", {"start": v(-7.07, -4.4) * mm, "end": v(-6.9, -4.27) * mm});
            skLineSegment(sketch, "E406", {"start": v(-6.9, -4.27) * mm, "end": v(-6.72, -4.14) * mm});
            skLineSegment(sketch, "E407", {"start": v(-6.72, -4.14) * mm, "end": v(-6.55, -4) * mm});
            skLineSegment(sketch, "E408", {"start": v(-6.55, -4) * mm, "end": v(-6.38, -3.87) * mm});
            skLineSegment(sketch, "E409", {"start": v(-6.38, -3.87) * mm, "end": v(-6.2, -3.74) * mm});
            skLineSegment(sketch, "E410", {"start": v(-6.2, -3.74) * mm, "end": v(-6.04, -3.9) * mm});
            skLineSegment(sketch, "E411", {"start": v(-6.04, -3.9) * mm, "end": v(-5.89, -4.06) * mm});
            skLineSegment(sketch, "E412", {"start": v(-5.89, -4.06) * mm, "end": v(-5.73, -4.22) * mm});
            skLineSegment(sketch, "E413", {"start": v(-5.73, -4.22) * mm, "end": v(-5.57, -4.38) * mm});
            skLineSegment(sketch, "E414", {"start": v(-5.57, -4.38) * mm, "end": v(-5.4, -4.53) * mm});
            skLineSegment(sketch, "E415", {"start": v(-5.4, -4.53) * mm, "end": v(-5.25, -4.7) * mm});
            skLineSegment(sketch, "E416", {"start": v(-5.25, -4.7) * mm, "end": v(-5.09, -4.85) * mm});
            skLineSegment(sketch, "E417", {"start": v(-5.09, -4.85) * mm, "end": v(-5.07, -4.87) * mm});
            skLineSegment(sketch, "E418", {"start": v(-5.07, -4.87) * mm, "end": v(-5.2, -5.04) * mm});
            skLineSegment(sketch, "E419", {"start": v(-5.2, -5.04) * mm, "end": v(-5.34, -5.22) * mm});
            skLineSegment(sketch, "E420", {"start": v(-5.34, -5.22) * mm, "end": v(-5.47, -5.4) * mm});
            skLineSegment(sketch, "E421", {"start": v(-5.47, -5.4) * mm, "end": v(-5.6, -5.56) * mm});
            skLineSegment(sketch, "E422", {"start": v(-5.6, -5.56) * mm, "end": v(-5.73, -5.74) * mm});
            skLineSegment(sketch, "E423", {"start": v(-5.73, -5.74) * mm, "end": v(-5.87, -5.9) * mm});
            skLineSegment(sketch, "E424", {"start": v(-5.87, -5.9) * mm, "end": v(-6, -6.08) * mm});
            skLineSegment(sketch, "E425", {"start": v(-6, -6.08) * mm, "end": v(-6.13, -6.25) * mm});
            skLineSegment(sketch, "E426", {"start": v(-6.13, -6.25) * mm, "end": v(-6.26, -6.43) * mm});
            skLineSegment(sketch, "E427", {"start": v(-6.26, -6.43) * mm, "end": v(-6.4, -6.6) * mm});
            skLineSegment(sketch, "E428", {"start": v(-6.4, -6.6) * mm, "end": v(-6.5, -6.8) * mm});
            skLineSegment(sketch, "E429", {"start": v(-6.5, -6.8) * mm, "end": v(-6.58, -7) * mm});
            skLineSegment(sketch, "E430", {"start": v(-6.58, -7) * mm, "end": v(-6.65, -7.22) * mm});
            skLineSegment(sketch, "E431", {"start": v(-6.65, -7.22) * mm, "end": v(-6.7, -7.43) * mm});
            skLineSegment(sketch, "E432", {"start": v(-6.7, -7.43) * mm, "end": v(-6.74, -7.65) * mm});
            skLineSegment(sketch, "E433", {"start": v(-6.74, -7.65) * mm, "end": v(-6.77, -7.86) * mm});
            skLineSegment(sketch, "E434", {"start": v(-6.77, -7.86) * mm, "end": v(-6.78, -8.09) * mm});
            skLineSegment(sketch, "E435", {"start": v(-6.78, -8.09) * mm, "end": v(-6.78, -8.3) * mm});
            skLineSegment(sketch, "E436", {"start": v(-6.78, -8.3) * mm, "end": v(-6.76, -8.53) * mm});
            skLineSegment(sketch, "E437", {"start": v(-6.76, -8.53) * mm, "end": v(-6.73, -8.74) * mm});
            skLineSegment(sketch, "E438", {"start": v(-6.73, -8.74) * mm, "end": v(-6.69, -8.96) * mm});
            skLineSegment(sketch, "E439", {"start": v(-6.69, -8.96) * mm, "end": v(-6.63, -9.17) * mm});
            skLineSegment(sketch, "E440", {"start": v(-6.63, -9.17) * mm, "end": v(-6.4, -9.12) * mm});
            skLineSegment(sketch, "E441", {"start": v(-6.4, -9.12) * mm, "end": v(-6.2, -9.05) * mm});
            skLineSegment(sketch, "E442", {"start": v(-6.2, -9.05) * mm, "end": v(-6, -8.96) * mm});
            skLineSegment(sketch, "E443", {"start": v(-6, -8.96) * mm, "end": v(-5.8, -8.87) * mm});
            skLineSegment(sketch, "E444", {"start": v(-5.8, -8.87) * mm, "end": v(-5.6, -8.76) * mm});
            skLineSegment(sketch, "E445", {"start": v(-5.6, -8.76) * mm, "end": v(-5.42, -8.64) * mm});
            skLineSegment(sketch, "E446", {"start": v(-5.42, -8.64) * mm, "end": v(-5.24, -8.5) * mm});
            skLineSegment(sketch, "E447", {"start": v(-5.24, -8.5) * mm, "end": v(-5.08, -8.36) * mm});
            skLineSegment(sketch, "E448", {"start": v(-5.08, -8.36) * mm, "end": v(-4.92, -8.2) * mm});
            skLineSegment(sketch, "E449", {"start": v(-4.92, -8.2) * mm, "end": v(-4.77, -8.04) * mm});
            skLineSegment(sketch, "E450", {"start": v(-4.77, -8.04) * mm, "end": v(-4.64, -7.86) * mm});
            skLineSegment(sketch, "E451", {"start": v(-4.64, -7.86) * mm, "end": v(-4.52, -7.69) * mm});
            skLineSegment(sketch, "E452", {"start": v(-4.52, -7.69) * mm, "end": v(-4.43, -7.48) * mm});
            skLineSegment(sketch, "E453", {"start": v(-4.43, -7.48) * mm, "end": v(-4.35, -7.28) * mm});
            skLineSegment(sketch, "E454", {"start": v(-4.35, -7.28) * mm, "end": v(-4.27, -7.08) * mm});
            skLineSegment(sketch, "E455", {"start": v(-4.27, -7.08) * mm, "end": v(-4.18, -6.88) * mm});
            skLineSegment(sketch, "E456", {"start": v(-4.18, -6.88) * mm, "end": v(-4.1, -6.68) * mm});
            skLineSegment(sketch, "E457", {"start": v(-4.1, -6.68) * mm, "end": v(-4.02, -6.48) * mm});
            skLineSegment(sketch, "E458", {"start": v(-4.02, -6.48) * mm, "end": v(-3.93, -6.28) * mm});
            skLineSegment(sketch, "E459", {"start": v(-3.93, -6.28) * mm, "end": v(-3.85, -6.08) * mm});
            skLineSegment(sketch, "E460", {"start": v(-3.85, -6.08) * mm, "end": v(-3.77, -5.87) * mm});
            skLineSegment(sketch, "E461", {"start": v(-3.77, -5.87) * mm, "end": v(-3.68, -5.67) * mm});
            skLineSegment(sketch, "E462", {"start": v(-3.68, -5.67) * mm, "end": v(-3.46, -5.73) * mm});
            skLineSegment(sketch, "E463", {"start": v(-3.46, -5.73) * mm, "end": v(-3.25, -5.8) * mm});
            skLineSegment(sketch, "E464", {"start": v(-3.25, -5.8) * mm, "end": v(-3.03, -5.85) * mm});
            skLineSegment(sketch, "E465", {"start": v(-3.03, -5.85) * mm, "end": v(-2.81, -5.9) * mm});
            skLineSegment(sketch, "E466", {"start": v(-2.81, -5.9) * mm, "end": v(-2.6, -5.97) * mm});
            skLineSegment(sketch, "E467", {"start": v(-2.6, -5.97) * mm, "end": v(-2.38, -6.02) * mm});
            skLineSegment(sketch, "E468", {"start": v(-2.38, -6.02) * mm, "end": v(-2.16, -6.08) * mm});
            skLineSegment(sketch, "E469", {"start": v(-2.16, -6.08) * mm, "end": v(-2.13, -6.09) * mm});
            skLineSegment(sketch, "E470", {"start": v(-2.13, -6.09) * mm, "end": v(-2.16, -6.3) * mm});
            skLineSegment(sketch, "E471", {"start": v(-2.16, -6.3) * mm, "end": v(-2.2, -6.52) * mm});
            skLineSegment(sketch, "E472", {"start": v(-2.2, -6.52) * mm, "end": v(-2.22, -6.74) * mm});
            skLineSegment(sketch, "E473", {"start": v(-2.22, -6.74) * mm, "end": v(-2.25, -6.95) * mm});
            skLineSegment(sketch, "E474", {"start": v(-2.25, -6.95) * mm, "end": v(-2.28, -7.17) * mm});
            skLineSegment(sketch, "E475", {"start": v(-2.28, -7.17) * mm, "end": v(-2.3, -7.38) * mm});
            skLineSegment(sketch, "E476", {"start": v(-2.3, -7.38) * mm, "end": v(-2.33, -7.6) * mm});
            skLineSegment(sketch, "E477", {"start": v(-2.33, -7.6) * mm, "end": v(-2.36, -7.82) * mm});
            skLineSegment(sketch, "E478", {"start": v(-2.36, -7.82) * mm, "end": v(-2.39, -8.03) * mm});
            skLineSegment(sketch, "E479", {"start": v(-2.39, -8.03) * mm, "end": v(-2.42, -8.25) * mm});
            skLineSegment(sketch, "E480", {"start": v(-2.42, -8.25) * mm, "end": v(-2.4, -8.47) * mm});
            skLineSegment(sketch, "E481", {"start": v(-2.4, -8.47) * mm, "end": v(-2.37, -8.69) * mm});
            skLineSegment(sketch, "E482", {"start": v(-2.37, -8.69) * mm, "end": v(-2.32, -8.9) * mm});
            skLineSegment(sketch, "E483", {"start": v(-2.32, -8.9) * mm, "end": v(-2.27, -9.12) * mm});
            skLineSegment(sketch, "E484", {"start": v(-2.27, -9.12) * mm, "end": v(-2.2, -9.33) * mm});
            skLineSegment(sketch, "E485", {"start": v(-2.2, -9.33) * mm, "end": v(-2.1, -9.53) * mm});
            skLineSegment(sketch, "E486", {"start": v(-2.1, -9.53) * mm, "end": v(-2, -9.73) * mm});
            skLineSegment(sketch, "E487", {"start": v(-2, -9.73) * mm, "end": v(-1.9, -9.92) * mm});
            skLineSegment(sketch, "E488", {"start": v(-1.9, -9.92) * mm, "end": v(-1.77, -10.1) * mm});
            skLineSegment(sketch, "E489", {"start": v(-1.77, -10.1) * mm, "end": v(-1.64, -10.27) * mm});
            skLineSegment(sketch, "E490", {"start": v(-1.64, -10.27) * mm, "end": v(-1.49, -10.44) * mm});
            skLineSegment(sketch, "E491", {"start": v(-1.49, -10.44) * mm, "end": v(-1.33, -10.6) * mm});
            skLineSegment(sketch, "E492", {"start": v(-1.33, -10.6) * mm, "end": v(-1.17, -10.43) * mm});
            skLineSegment(sketch, "E493", {"start": v(-1.17, -10.43) * mm, "end": v(-1.03, -10.27) * mm});
            skLineSegment(sketch, "E494", {"start": v(-1.03, -10.27) * mm, "end": v(-0.89, -10.1) * mm});
            skLineSegment(sketch, "E495", {"start": v(-0.89, -10.1) * mm, "end": v(-0.77, -9.92) * mm});
            skLineSegment(sketch, "E496", {"start": v(-0.77, -9.92) * mm, "end": v(-0.65, -9.72) * mm});
            skLineSegment(sketch, "E497", {"start": v(-0.65, -9.72) * mm, "end": v(-0.55, -9.53) * mm});
            skLineSegment(sketch, "E498", {"start": v(-0.55, -9.53) * mm, "end": v(-0.47, -9.32) * mm});
            skLineSegment(sketch, "E499", {"start": v(-0.47, -9.32) * mm, "end": v(-0.4, -9.12) * mm});
            skLineSegment(sketch, "E500", {"start": v(-0.4, -9.12) * mm, "end": v(-0.34, -8.9) * mm});
            skLineSegment(sketch, "E501", {"start": v(-0.34, -8.9) * mm, "end": v(-0.3, -8.69) * mm});
            skLineSegment(sketch, "E502", {"start": v(-0.3, -8.69) * mm, "end": v(-0.26, -8.46) * mm});
            skLineSegment(sketch, "E503", {"start": v(-0.26, -8.46) * mm, "end": v(-0.25, -8.25) * mm});
            skLineSegment(sketch, "E504", {"start": v(-0.25, -8.25) * mm, "end": v(-0.27, -8.03) * mm});
            skLineSegment(sketch, "E505", {"start": v(-0.27, -8.03) * mm, "end": v(-0.3, -7.82) * mm});
            skLineSegment(sketch, "E506", {"start": v(-0.3, -7.82) * mm, "end": v(-0.33, -7.6) * mm});
            skLineSegment(sketch, "E507", {"start": v(-0.33, -7.6) * mm, "end": v(-0.36, -7.38) * mm});
            skLineSegment(sketch, "E508", {"start": v(-0.36, -7.38) * mm, "end": v(-0.39, -7.17) * mm});
            skLineSegment(sketch, "E509", {"start": v(-0.39, -7.17) * mm, "end": v(-0.42, -6.95) * mm});
            skLineSegment(sketch, "E510", {"start": v(-0.42, -6.95) * mm, "end": v(-0.44, -6.74) * mm});
            skLineSegment(sketch, "E511", {"start": v(-0.44, -6.74) * mm, "end": v(-0.47, -6.52) * mm});
            skLineSegment(sketch, "E512", {"start": v(-0.47, -6.52) * mm, "end": v(-0.5, -6.3) * mm});
            skLineSegment(sketch, "E513", {"start": v(-0.5, -6.3) * mm, "end": v(-0.53, -6.09) * mm});
            skLineSegment(sketch, "E514", {"start": v(-0.53, -6.09) * mm, "end": v(-0.31, -6.03) * mm});
            skLineSegment(sketch, "E515", {"start": v(-0.31, -6.03) * mm, "end": v(-0.1, -5.97) * mm});
            skLineSegment(sketch, "E516", {"start": v(-0.1, -5.97) * mm, "end": v(0.12, -5.91) * mm});
            skLineSegment(sketch, "E517", {"start": v(0.12, -5.91) * mm, "end": v(0.34, -5.86) * mm});
            skLineSegment(sketch, "E518", {"start": v(0.34, -5.86) * mm, "end": v(0.56, -5.8) * mm});
            skLineSegment(sketch, "E519", {"start": v(0.56, -5.8) * mm, "end": v(0.78, -5.74) * mm});
            skLineSegment(sketch, "E520", {"start": v(0.78, -5.74) * mm, "end": v(1, -5.68) * mm});
            skLineSegment(sketch, "E521", {"start": v(1, -5.68) * mm, "end": v(1.02, -5.67) * mm});
            skLineSegment(sketch, "E522", {"start": v(1.02, -5.67) * mm, "end": v(1.1, -5.87) * mm});
            skLineSegment(sketch, "E523", {"start": v(1.1, -5.87) * mm, "end": v(1.18, -6.08) * mm});
            skLineSegment(sketch, "E524", {"start": v(1.18, -6.08) * mm, "end": v(1.27, -6.28) * mm});
            skLineSegment(sketch, "E525", {"start": v(1.27, -6.28) * mm, "end": v(1.35, -6.48) * mm});
            skLineSegment(sketch, "E526", {"start": v(1.35, -6.48) * mm, "end": v(1.44, -6.68) * mm});
            skLineSegment(sketch, "E527", {"start": v(1.44, -6.68) * mm, "end": v(1.52, -6.88) * mm});
            skLineSegment(sketch, "E528", {"start": v(1.52, -6.88) * mm, "end": v(1.6, -7.08) * mm});
            skLineSegment(sketch, "E529", {"start": v(1.6, -7.08) * mm, "end": v(1.69, -7.28) * mm});
            skLineSegment(sketch, "E530", {"start": v(1.69, -7.28) * mm, "end": v(1.77, -7.48) * mm});
            skLineSegment(sketch, "E531", {"start": v(1.77, -7.48) * mm, "end": v(1.85, -7.69) * mm});
            skLineSegment(sketch, "E532", {"start": v(1.85, -7.69) * mm, "end": v(1.98, -7.87) * mm});
            skLineSegment(sketch, "E533", {"start": v(1.98, -7.87) * mm, "end": v(2.11, -8.04) * mm});
            skLineSegment(sketch, "E534", {"start": v(2.11, -8.04) * mm, "end": v(2.26, -8.21) * mm});
            skLineSegment(sketch, "E535", {"start": v(2.26, -8.21) * mm, "end": v(2.42, -8.36) * mm});
            skLineSegment(sketch, "E536", {"start": v(2.42, -8.36) * mm, "end": v(2.59, -8.5) * mm});
            skLineSegment(sketch, "E537", {"start": v(2.59, -8.5) * mm, "end": v(2.76, -8.64) * mm});
            skLineSegment(sketch, "E538", {"start": v(2.76, -8.64) * mm, "end": v(2.95, -8.76) * mm});
            skLineSegment(sketch, "E539", {"start": v(2.95, -8.76) * mm, "end": v(3.14, -8.87) * mm});
            skLineSegment(sketch, "E540", {"start": v(3.14, -8.87) * mm, "end": v(3.34, -8.97) * mm});
            skLineSegment(sketch, "E541", {"start": v(3.34, -8.97) * mm, "end": v(3.54, -9.05) * mm});
            skLineSegment(sketch, "E542", {"start": v(3.54, -9.05) * mm, "end": v(3.75, -9.12) * mm});
            skLineSegment(sketch, "E543", {"start": v(3.75, -9.12) * mm, "end": v(3.96, -9.17) * mm});
            skLineSegment(sketch, "E544", {"start": v(3.96, -9.17) * mm, "end": v(4.02, -8.96) * mm});
            skLineSegment(sketch, "E545", {"start": v(4.02, -8.96) * mm, "end": v(4.07, -8.74) * mm});
            skLineSegment(sketch, "E546", {"start": v(4.07, -8.74) * mm, "end": v(4.1, -8.52) * mm});
            skLineSegment(sketch, "E547", {"start": v(4.1, -8.52) * mm, "end": v(4.12, -8.3) * mm});
            skLineSegment(sketch, "E548", {"start": v(4.12, -8.3) * mm, "end": v(4.12, -8.08) * mm});
            skLineSegment(sketch, "E549", {"start": v(4.12, -8.08) * mm, "end": v(4.1, -7.86) * mm});
            skLineSegment(sketch, "E550", {"start": v(4.1, -7.86) * mm, "end": v(4.08, -7.64) * mm});
            skLineSegment(sketch, "E551", {"start": v(4.08, -7.64) * mm, "end": v(4.04, -7.43) * mm});
            skLineSegment(sketch, "E552", {"start": v(4.04, -7.43) * mm, "end": v(3.98, -7.2) * mm});
            skLineSegment(sketch, "E553", {"start": v(3.98, -7.2) * mm, "end": v(3.91, -7) * mm});
            skLineSegment(sketch, "E554", {"start": v(3.91, -7) * mm, "end": v(3.83, -6.8) * mm});
            skLineSegment(sketch, "E555", {"start": v(3.83, -6.8) * mm, "end": v(3.73, -6.6) * mm});
            skLineSegment(sketch, "E556", {"start": v(3.73, -6.6) * mm, "end": v(3.6, -6.43) * mm});
            skLineSegment(sketch, "E557", {"start": v(3.6, -6.43) * mm, "end": v(3.47, -6.25) * mm});
            skLineSegment(sketch, "E558", {"start": v(3.47, -6.25) * mm, "end": v(3.33, -6.08) * mm});
            skLineSegment(sketch, "E559", {"start": v(3.33, -6.08) * mm, "end": v(3.2, -5.9) * mm});
            skLineSegment(sketch, "E560", {"start": v(3.2, -5.9) * mm, "end": v(3.07, -5.74) * mm});
            skLineSegment(sketch, "E561", {"start": v(3.07, -5.74) * mm, "end": v(2.94, -5.56) * mm});
            skLineSegment(sketch, "E562", {"start": v(2.94, -5.56) * mm, "end": v(2.8, -5.4) * mm});
            skLineSegment(sketch, "E563", {"start": v(2.8, -5.4) * mm, "end": v(2.67, -5.22) * mm});
            skLineSegment(sketch, "E564", {"start": v(2.67, -5.22) * mm, "end": v(2.54, -5.04) * mm});
            skLineSegment(sketch, "E565", {"start": v(2.54, -5.04) * mm, "end": v(2.4, -4.87) * mm});
            skLineSegment(sketch, "E566", {"start": v(2.4, -4.87) * mm, "end": v(2.57, -4.71) * mm});
            skLineSegment(sketch, "E567", {"start": v(2.57, -4.71) * mm, "end": v(2.73, -4.55) * mm});
            skLineSegment(sketch, "E568", {"start": v(2.73, -4.55) * mm, "end": v(2.88, -4.4) * mm});
            skLineSegment(sketch, "E569", {"start": v(2.88, -4.4) * mm, "end": v(3.04, -4.23) * mm});
            skLineSegment(sketch, "E570", {"start": v(3.04, -4.23) * mm, "end": v(3.2, -4.08) * mm});
            skLineSegment(sketch, "E571", {"start": v(3.2, -4.08) * mm, "end": v(3.36, -3.92) * mm});
            skLineSegment(sketch, "E572", {"start": v(3.36, -3.92) * mm, "end": v(3.52, -3.76) * mm});
            skLineSegment(sketch, "E573", {"start": v(3.52, -3.76) * mm, "end": v(3.54, -3.74) * mm});
            skLineSegment(sketch, "E574", {"start": v(3.54, -3.74) * mm, "end": v(3.71, -3.87) * mm});
            skLineSegment(sketch, "E575", {"start": v(3.71, -3.87) * mm, "end": v(3.89, -4) * mm});
            skLineSegment(sketch, "E576", {"start": v(3.89, -4) * mm, "end": v(4.06, -4.14) * mm});
            skLineSegment(sketch, "E577", {"start": v(4.06, -4.14) * mm, "end": v(4.23, -4.27) * mm});
            skLineSegment(sketch, "E578", {"start": v(4.23, -4.27) * mm, "end": v(4.4, -4.4) * mm});
            skLineSegment(sketch, "E579", {"start": v(4.4, -4.4) * mm, "end": v(4.58, -4.53) * mm});
            skLineSegment(sketch, "E580", {"start": v(4.58, -4.53) * mm, "end": v(4.75, -4.67) * mm});
            skLineSegment(sketch, "E581", {"start": v(4.75, -4.67) * mm, "end": v(4.92, -4.8) * mm});
            skLineSegment(sketch, "E582", {"start": v(4.92, -4.8) * mm, "end": v(5.1, -4.93) * mm});
            skLineSegment(sketch, "E583", {"start": v(5.1, -4.93) * mm, "end": v(5.27, -5.06) * mm});
            skLineSegment(sketch, "E584", {"start": v(5.27, -5.06) * mm, "end": v(5.47, -5.16) * mm});
            skLineSegment(sketch, "E585", {"start": v(5.47, -5.16) * mm, "end": v(5.67, -5.24) * mm});
            skLineSegment(sketch, "E586", {"start": v(5.67, -5.24) * mm, "end": v(5.89, -5.31) * mm});
            skLineSegment(sketch, "E587", {"start": v(5.89, -5.31) * mm, "end": v(6.1, -5.37) * mm});
            skLineSegment(sketch, "E588", {"start": v(6.1, -5.37) * mm, "end": v(6.32, -5.41) * mm});
            skLineSegment(sketch, "E589", {"start": v(6.32, -5.41) * mm, "end": v(6.53, -5.44) * mm});
            skLineSegment(sketch, "E590", {"start": v(6.53, -5.44) * mm, "end": v(6.76, -5.45) * mm});
            skLineSegment(sketch, "E591", {"start": v(6.76, -5.45) * mm, "end": v(6.97, -5.45) * mm});
            skLineSegment(sketch, "E592", {"start": v(6.97, -5.45) * mm, "end": v(7.2, -5.43) * mm});
            skLineSegment(sketch, "E593", {"start": v(7.2, -5.43) * mm, "end": v(7.41, -5.4) * mm});
            skLineSegment(sketch, "E594", {"start": v(7.41, -5.4) * mm, "end": v(7.63, -5.35) * mm});
            skLineSegment(sketch, "E595", {"start": v(7.63, -5.35) * mm, "end": v(7.84, -5.3) * mm});
            skLineSegment(sketch, "E596", {"start": v(7.84, -5.3) * mm, "end": v(7.78, -5.08) * mm});
            skLineSegment(sketch, "E597", {"start": v(7.78, -5.08) * mm, "end": v(7.72, -4.87) * mm});
            skLineSegment(sketch, "E598", {"start": v(7.72, -4.87) * mm, "end": v(7.63, -4.66) * mm});
            skLineSegment(sketch, "E599", {"start": v(7.63, -4.66) * mm, "end": v(7.54, -4.47) * mm});
            skLineSegment(sketch, "E600", {"start": v(7.54, -4.47) * mm, "end": v(7.43, -4.27) * mm});
            skLineSegment(sketch, "E601", {"start": v(7.43, -4.27) * mm, "end": v(7.3, -4.1) * mm});
            skLineSegment(sketch, "E602", {"start": v(7.3, -4.1) * mm, "end": v(7.17, -3.91) * mm});
            skLineSegment(sketch, "E603", {"start": v(7.17, -3.91) * mm, "end": v(7.03, -3.75) * mm});
            skLineSegment(sketch, "E604", {"start": v(7.03, -3.75) * mm, "end": v(6.87, -3.59) * mm});
            skLineSegment(sketch, "E605", {"start": v(6.87, -3.59) * mm, "end": v(6.71, -3.44) * mm});
            skLineSegment(sketch, "E606", {"start": v(6.71, -3.44) * mm, "end": v(6.53, -3.3) * mm});
            skLineSegment(sketch, "E607", {"start": v(6.53, -3.3) * mm, "end": v(6.35, -3.18) * mm});
            skLineSegment(sketch, "E608", {"start": v(6.35, -3.18) * mm, "end": v(6.15, -3.1) * mm});
            skLineSegment(sketch, "E609", {"start": v(6.15, -3.1) * mm, "end": v(5.95, -3.02) * mm});
            skLineSegment(sketch, "E610", {"start": v(5.95, -3.02) * mm, "end": v(5.75, -2.93) * mm});
            skLineSegment(sketch, "E611", {"start": v(5.75, -2.93) * mm, "end": v(5.55, -2.85) * mm});
            skLineSegment(sketch, "E612", {"start": v(5.55, -2.85) * mm, "end": v(5.35, -2.77) * mm});
            skLineSegment(sketch, "E613", {"start": v(5.35, -2.77) * mm, "end": v(5.15, -2.68) * mm});
            skLineSegment(sketch, "E614", {"start": v(5.15, -2.68) * mm, "end": v(4.95, -2.6) * mm});
            skLineSegment(sketch, "E615", {"start": v(4.95, -2.6) * mm, "end": v(4.74, -2.52) * mm});
            skLineSegment(sketch, "E616", {"start": v(4.74, -2.52) * mm, "end": v(4.54, -2.43) * mm});
            skLineSegment(sketch, "E617", {"start": v(4.54, -2.43) * mm, "end": v(4.34, -2.35) * mm});
            skLineSegment(sketch, "E618", {"start": v(4.34, -2.35) * mm, "end": v(4.4, -2.13) * mm});
            skLineSegment(sketch, "E619", {"start": v(4.4, -2.13) * mm, "end": v(4.46, -1.91) * mm});
            skLineSegment(sketch, "E620", {"start": v(4.46, -1.91) * mm, "end": v(4.52, -1.7) * mm});
            skLineSegment(sketch, "E621", {"start": v(4.52, -1.7) * mm, "end": v(4.58, -1.48) * mm});
            skLineSegment(sketch, "E622", {"start": v(4.58, -1.48) * mm, "end": v(4.63, -1.26) * mm});
            skLineSegment(sketch, "E623", {"start": v(4.63, -1.26) * mm, "end": v(4.7, -1.04) * mm});
            skLineSegment(sketch, "E624", {"start": v(4.7, -1.04) * mm, "end": v(4.75, -0.83) * mm});
            skLineSegment(sketch, "E625", {"start": v(4.75, -0.83) * mm, "end": v(4.76, -0.8) * mm});
            skCircle(sketch, "E626", {"center": v(-1.33, 0) * mm, "radius": 2.65 * mm});
            skSolve(sketch);
        }
        {
            var Q0;
            Q0=makeQuery(id+"F0.imprint","IMPRINT",FACE,{"disambiguationData":[TD([[makeQuery(id+"F0.imprint","IMPRINT",EDGE,{"derivedFrom":sQuery(id+"F0.wireOp",EDGE,"E0")}),1.0]])]});
            extrude(context, id + "F1", {"entities" : qUnion([Q0]), "depth" : 8 * mm});
        }
        {
            var Q0;
            Q0=makeQuery(id+"F1.opExtrude","CAP_FACE",FACE,{"disambiguationData":[OSD([sQuery(id+"F0.wireOp",EDGE,"E0"),sQuery(id+"F0.wireOp",EDGE,"E1"),sQuery(id+"F0.wireOp",EDGE,"E2"),sQuery(id+"F0.wireOp",EDGE,"E3"),sQuery(id+"F0.wireOp",EDGE,"E4"),sQuery(id+"F0.wireOp",EDGE,"E5"),sQuery(id+"F0.wireOp",EDGE,"E6"),sQuery(id+"F0.wireOp",EDGE,"E7"),sQuery(id+"F0.wireOp",EDGE,"E8"),sQuery(id+"F0.wireOp",EDGE,"E9"),sQuery(id+"F0.wireOp",EDGE,"E10"),sQuery(id+"F0.wireOp",EDGE,"E11"),sQuery(id+"F0.wireOp",EDGE,"E12"),sQuery(id+"F0.wireOp",EDGE,"E13"),sQuery(id+"F0.wireOp",EDGE,"E14"),sQuery(id+"F0.wireOp",EDGE,"E15"),sQuery(id+"F0.wireOp",EDGE,"E16"),sQuery(id+"F0.wireOp",EDGE,"E17"),sQuery(id+"F0.wireOp",EDGE,"E18"),sQuery(id+"F0.wireOp",EDGE,"E19"),sQuery(id+"F0.wireOp",EDGE,"E20"),sQuery(id+"F0.wireOp",EDGE,"E21"),sQuery(id+"F0.wireOp",EDGE,"E22"),sQuery(id+"F0.wireOp",EDGE,"E23"),sQuery(id+"F0.wireOp",EDGE,"E24"),sQuery(id+"F0.wireOp",EDGE,"E25"),sQuery(id+"F0.wireOp",EDGE,"E26"),sQuery(id+"F0.wireOp",EDGE,"E27"),sQuery(id+"F0.wireOp",EDGE,"E28"),sQuery(id+"F0.wireOp",EDGE,"E29"),sQuery(id+"F0.wireOp",EDGE,"E30"),sQuery(id+"F0.wireOp",EDGE,"E31"),sQuery(id+"F0.wireOp",EDGE,"E32"),sQuery(id+"F0.wireOp",EDGE,"E33"),sQuery(id+"F0.wireOp",EDGE,"E34"),sQuery(id+"F0.wireOp",EDGE,"E35"),sQuery(id+"F0.wireOp",EDGE,"E36"),sQuery(id+"F0.wireOp",EDGE,"E37"),sQuery(id+"F0.wireOp",EDGE,"E38"),sQuery(id+"F0.wireOp",EDGE,"E39"),sQuery(id+"F0.wireOp",EDGE,"E40"),sQuery(id+"F0.wireOp",EDGE,"E41"),sQuery(id+"F0.wireOp",EDGE,"E42"),sQuery(id+"F0.wireOp",EDGE,"E43"),sQuery(id+"F0.wireOp",EDGE,"E44"),sQuery(id+"F0.wireOp",EDGE,"E45"),sQuery(id+"F0.wireOp",EDGE,"E46"),sQuery(id+"F0.wireOp",EDGE,"E47"),sQuery(id+"F0.wireOp",EDGE,"E48"),sQuery(id+"F0.wireOp",EDGE,"E49"),sQuery(id+"F0.wireOp",EDGE,"E50"),sQuery(id+"F0.wireOp",EDGE,"E51"),sQuery(id+"F0.wireOp",EDGE,"E52"),sQuery(id+"F0.wireOp",EDGE,"E53"),sQuery(id+"F0.wireOp",EDGE,"E54"),sQuery(id+"F0.wireOp",EDGE,"E55"),sQuery(id+"F0.wireOp",EDGE,"E56"),sQuery(id+"F0.wireOp",EDGE,"E57"),sQuery(id+"F0.wireOp",EDGE,"E58"),sQuery(id+"F0.wireOp",EDGE,"E59"),sQuery(id+"F0.wireOp",EDGE,"E60"),sQuery(id+"F0.wireOp",EDGE,"E61"),sQuery(id+"F0.wireOp",EDGE,"E62"),sQuery(id+"F0.wireOp",EDGE,"E63"),sQuery(id+"F0.wireOp",EDGE,"E64"),sQuery(id+"F0.wireOp",EDGE,"E65"),sQuery(id+"F0.wireOp",EDGE,"E66"),sQuery(id+"F0.wireOp",EDGE,"E67"),sQuery(id+"F0.wireOp",EDGE,"E68"),sQuery(id+"F0.wireOp",EDGE,"E69"),sQuery(id+"F0.wireOp",EDGE,"E70"),sQuery(id+"F0.wireOp",EDGE,"E71"),sQuery(id+"F0.wireOp",EDGE,"E72"),sQuery(id+"F0.wireOp",EDGE,"E73"),sQuery(id+"F0.wireOp",EDGE,"E74"),sQuery(id+"F0.wireOp",EDGE,"E75"),sQuery(id+"F0.wireOp",EDGE,"E76"),sQuery(id+"F0.wireOp",EDGE,"E77"),sQuery(id+"F0.wireOp",EDGE,"E78"),sQuery(id+"F0.wireOp",EDGE,"E79"),sQuery(id+"F0.wireOp",EDGE,"E80"),sQuery(id+"F0.wireOp",EDGE,"E81"),sQuery(id+"F0.wireOp",EDGE,"E82"),sQuery(id+"F0.wireOp",EDGE,"E83"),sQuery(id+"F0.wireOp",EDGE,"E84"),sQuery(id+"F0.wireOp",EDGE,"E85"),sQuery(id+"F0.wireOp",EDGE,"E86"),sQuery(id+"F0.wireOp",EDGE,"E87"),sQuery(id+"F0.wireOp",EDGE,"E88"),sQuery(id+"F0.wireOp",EDGE,"E89"),sQuery(id+"F0.wireOp",EDGE,"E90"),sQuery(id+"F0.wireOp",EDGE,"E91"),sQuery(id+"F0.wireOp",EDGE,"E92"),sQuery(id+"F0.wireOp",EDGE,"E93"),sQuery(id+"F0.wireOp",EDGE,"E94"),sQuery(id+"F0.wireOp",EDGE,"E95"),sQuery(id+"F0.wireOp",EDGE,"E96"),sQuery(id+"F0.wireOp",EDGE,"E97"),sQuery(id+"F0.wireOp",EDGE,"E98"),sQuery(id+"F0.wireOp",EDGE,"E99"),sQuery(id+"F0.wireOp",EDGE,"E100"),sQuery(id+"F0.wireOp",EDGE,"E101"),sQuery(id+"F0.wireOp",EDGE,"E102"),sQuery(id+"F0.wireOp",EDGE,"E103"),sQuery(id+"F0.wireOp",EDGE,"E104"),sQuery(id+"F0.wireOp",EDGE,"E105"),sQuery(id+"F0.wireOp",EDGE,"E106"),sQuery(id+"F0.wireOp",EDGE,"E107"),sQuery(id+"F0.wireOp",EDGE,"E108"),sQuery(id+"F0.wireOp",EDGE,"E109"),sQuery(id+"F0.wireOp",EDGE,"E110"),sQuery(id+"F0.wireOp",EDGE,"E111"),sQuery(id+"F0.wireOp",EDGE,"E112"),sQuery(id+"F0.wireOp",EDGE,"E113"),sQuery(id+"F0.wireOp",EDGE,"E114"),sQuery(id+"F0.wireOp",EDGE,"E115"),sQuery(id+"F0.wireOp",EDGE,"E116"),sQuery(id+"F0.wireOp",EDGE,"E117"),sQuery(id+"F0.wireOp",EDGE,"E118"),sQuery(id+"F0.wireOp",EDGE,"E119"),sQuery(id+"F0.wireOp",EDGE,"E120"),sQuery(id+"F0.wireOp",EDGE,"E121"),sQuery(id+"F0.wireOp",EDGE,"E122"),sQuery(id+"F0.wireOp",EDGE,"E123"),sQuery(id+"F0.wireOp",EDGE,"E124"),sQuery(id+"F0.wireOp",EDGE,"E125"),sQuery(id+"F0.wireOp",EDGE,"E126"),sQuery(id+"F0.wireOp",EDGE,"E127"),sQuery(id+"F0.wireOp",EDGE,"E128"),sQuery(id+"F0.wireOp",EDGE,"E129"),sQuery(id+"F0.wireOp",EDGE,"E130"),sQuery(id+"F0.wireOp",EDGE,"E131"),sQuery(id+"F0.wireOp",EDGE,"E132"),sQuery(id+"F0.wireOp",EDGE,"E133"),sQuery(id+"F0.wireOp",EDGE,"E134"),sQuery(id+"F0.wireOp",EDGE,"E135"),sQuery(id+"F0.wireOp",EDGE,"E136"),sQuery(id+"F0.wireOp",EDGE,"E137"),sQuery(id+"F0.wireOp",EDGE,"E138"),sQuery(id+"F0.wireOp",EDGE,"E139"),sQuery(id+"F0.wireOp",EDGE,"E140"),sQuery(id+"F0.wireOp",EDGE,"E141"),sQuery(id+"F0.wireOp",EDGE,"E142"),sQuery(id+"F0.wireOp",EDGE,"E143"),sQuery(id+"F0.wireOp",EDGE,"E144"),sQuery(id+"F0.wireOp",EDGE,"E145"),sQuery(id+"F0.wireOp",EDGE,"E146"),sQuery(id+"F0.wireOp",EDGE,"E147"),sQuery(id+"F0.wireOp",EDGE,"E148"),sQuery(id+"F0.wireOp",EDGE,"E149"),sQuery(id+"F0.wireOp",EDGE,"E150"),sQuery(id+"F0.wireOp",EDGE,"E151"),sQuery(id+"F0.wireOp",EDGE,"E152"),sQuery(id+"F0.wireOp",EDGE,"E153"),sQuery(id+"F0.wireOp",EDGE,"E154"),sQuery(id+"F0.wireOp",EDGE,"E155"),sQuery(id+"F0.wireOp",EDGE,"E156"),sQuery(id+"F0.wireOp",EDGE,"E157"),sQuery(id+"F0.wireOp",EDGE,"E158"),sQuery(id+"F0.wireOp",EDGE,"E159"),sQuery(id+"F0.wireOp",EDGE,"E160"),sQuery(id+"F0.wireOp",EDGE,"E161"),sQuery(id+"F0.wireOp",EDGE,"E162"),sQuery(id+"F0.wireOp",EDGE,"E163"),sQuery(id+"F0.wireOp",EDGE,"E164"),sQuery(id+"F0.wireOp",EDGE,"E165"),sQuery(id+"F0.wireOp",EDGE,"E166"),sQuery(id+"F0.wireOp",EDGE,"E167"),sQuery(id+"F0.wireOp",EDGE,"E168"),sQuery(id+"F0.wireOp",EDGE,"E169"),sQuery(id+"F0.wireOp",EDGE,"E170"),sQuery(id+"F0.wireOp",EDGE,"E171"),sQuery(id+"F0.wireOp",EDGE,"E172"),sQuery(id+"F0.wireOp",EDGE,"E173"),sQuery(id+"F0.wireOp",EDGE,"E174"),sQuery(id+"F0.wireOp",EDGE,"E175"),sQuery(id+"F0.wireOp",EDGE,"E176"),sQuery(id+"F0.wireOp",EDGE,"E177"),sQuery(id+"F0.wireOp",EDGE,"E178"),sQuery(id+"F0.wireOp",EDGE,"E179"),sQuery(id+"F0.wireOp",EDGE,"E180"),sQuery(id+"F0.wireOp",EDGE,"E181"),sQuery(id+"F0.wireOp",EDGE,"E182"),sQuery(id+"F0.wireOp",EDGE,"E183"),sQuery(id+"F0.wireOp",EDGE,"E184"),sQuery(id+"F0.wireOp",EDGE,"E185"),sQuery(id+"F0.wireOp",EDGE,"E186"),sQuery(id+"F0.wireOp",EDGE,"E187"),sQuery(id+"F0.wireOp",EDGE,"E188"),sQuery(id+"F0.wireOp",EDGE,"E189"),sQuery(id+"F0.wireOp",EDGE,"E190"),sQuery(id+"F0.wireOp",EDGE,"E191"),sQuery(id+"F0.wireOp",EDGE,"E192"),sQuery(id+"F0.wireOp",EDGE,"E193"),sQuery(id+"F0.wireOp",EDGE,"E194"),sQuery(id+"F0.wireOp",EDGE,"E195"),sQuery(id+"F0.wireOp",EDGE,"E196"),sQuery(id+"F0.wireOp",EDGE,"E197"),sQuery(id+"F0.wireOp",EDGE,"E198"),sQuery(id+"F0.wireOp",EDGE,"E199"),sQuery(id+"F0.wireOp",EDGE,"E200"),sQuery(id+"F0.wireOp",EDGE,"E201"),sQuery(id+"F0.wireOp",EDGE,"E202"),sQuery(id+"F0.wireOp",EDGE,"E203"),sQuery(id+"F0.wireOp",EDGE,"E204"),sQuery(id+"F0.wireOp",EDGE,"E205"),sQuery(id+"F0.wireOp",EDGE,"E206"),sQuery(id+"F0.wireOp",EDGE,"E207"),sQuery(id+"F0.wireOp",EDGE,"E208"),sQuery(id+"F0.wireOp",EDGE,"E209"),sQuery(id+"F0.wireOp",EDGE,"E210"),sQuery(id+"F0.wireOp",EDGE,"E211"),sQuery(id+"F0.wireOp",EDGE,"E212"),sQuery(id+"F0.wireOp",EDGE,"E213"),sQuery(id+"F0.wireOp",EDGE,"E214"),sQuery(id+"F0.wireOp",EDGE,"E215"),sQuery(id+"F0.wireOp",EDGE,"E216"),sQuery(id+"F0.wireOp",EDGE,"E217"),sQuery(id+"F0.wireOp",EDGE,"E218"),sQuery(id+"F0.wireOp",EDGE,"E219"),sQuery(id+"F0.wireOp",EDGE,"E220"),sQuery(id+"F0.wireOp",EDGE,"E221"),sQuery(id+"F0.wireOp",EDGE,"E222"),sQuery(id+"F0.wireOp",EDGE,"E223"),sQuery(id+"F0.wireOp",EDGE,"E224"),sQuery(id+"F0.wireOp",EDGE,"E225"),sQuery(id+"F0.wireOp",EDGE,"E226"),sQuery(id+"F0.wireOp",EDGE,"E227"),sQuery(id+"F0.wireOp",EDGE,"E228"),sQuery(id+"F0.wireOp",EDGE,"E229"),sQuery(id+"F0.wireOp",EDGE,"E230"),sQuery(id+"F0.wireOp",EDGE,"E231"),sQuery(id+"F0.wireOp",EDGE,"E232"),sQuery(id+"F0.wireOp",EDGE,"E233"),sQuery(id+"F0.wireOp",EDGE,"E234"),sQuery(id+"F0.wireOp",EDGE,"E235"),sQuery(id+"F0.wireOp",EDGE,"E236"),sQuery(id+"F0.wireOp",EDGE,"E237"),sQuery(id+"F0.wireOp",EDGE,"E238"),sQuery(id+"F0.wireOp",EDGE,"E239"),sQuery(id+"F0.wireOp",EDGE,"E240"),sQuery(id+"F0.wireOp",EDGE,"E241"),sQuery(id+"F0.wireOp",EDGE,"E242"),sQuery(id+"F0.wireOp",EDGE,"E243"),sQuery(id+"F0.wireOp",EDGE,"E244"),sQuery(id+"F0.wireOp",EDGE,"E245"),sQuery(id+"F0.wireOp",EDGE,"E246"),sQuery(id+"F0.wireOp",EDGE,"E247"),sQuery(id+"F0.wireOp",EDGE,"E248"),sQuery(id+"F0.wireOp",EDGE,"E249"),sQuery(id+"F0.wireOp",EDGE,"E250"),sQuery(id+"F0.wireOp",EDGE,"E251"),sQuery(id+"F0.wireOp",EDGE,"E252"),sQuery(id+"F0.wireOp",EDGE,"E253"),sQuery(id+"F0.wireOp",EDGE,"E254"),sQuery(id+"F0.wireOp",EDGE,"E255"),sQuery(id+"F0.wireOp",EDGE,"E256"),sQuery(id+"F0.wireOp",EDGE,"E257"),sQuery(id+"F0.wireOp",EDGE,"E258"),sQuery(id+"F0.wireOp",EDGE,"E259"),sQuery(id+"F0.wireOp",EDGE,"E260"),sQuery(id+"F0.wireOp",EDGE,"E261"),sQuery(id+"F0.wireOp",EDGE,"E262"),sQuery(id+"F0.wireOp",EDGE,"E263"),sQuery(id+"F0.wireOp",EDGE,"E264"),sQuery(id+"F0.wireOp",EDGE,"E265"),sQuery(id+"F0.wireOp",EDGE,"E266"),sQuery(id+"F0.wireOp",EDGE,"E267"),sQuery(id+"F0.wireOp",EDGE,"E268"),sQuery(id+"F0.wireOp",EDGE,"E269"),sQuery(id+"F0.wireOp",EDGE,"E270"),sQuery(id+"F0.wireOp",EDGE,"E271"),sQuery(id+"F0.wireOp",EDGE,"E272"),sQuery(id+"F0.wireOp",EDGE,"E273"),sQuery(id+"F0.wireOp",EDGE,"E274"),sQuery(id+"F0.wireOp",EDGE,"E275"),sQuery(id+"F0.wireOp",EDGE,"E276"),sQuery(id+"F0.wireOp",EDGE,"E277"),sQuery(id+"F0.wireOp",EDGE,"E278"),sQuery(id+"F0.wireOp",EDGE,"E279"),sQuery(id+"F0.wireOp",EDGE,"E280"),sQuery(id+"F0.wireOp",EDGE,"E281"),sQuery(id+"F0.wireOp",EDGE,"E282"),sQuery(id+"F0.wireOp",EDGE,"E283"),sQuery(id+"F0.wireOp",EDGE,"E284"),sQuery(id+"F0.wireOp",EDGE,"E285"),sQuery(id+"F0.wireOp",EDGE,"E286"),sQuery(id+"F0.wireOp",EDGE,"E287"),sQuery(id+"F0.wireOp",EDGE,"E288"),sQuery(id+"F0.wireOp",EDGE,"E289"),sQuery(id+"F0.wireOp",EDGE,"E290"),sQuery(id+"F0.wireOp",EDGE,"E291"),sQuery(id+"F0.wireOp",EDGE,"E292"),sQuery(id+"F0.wireOp",EDGE,"E293"),sQuery(id+"F0.wireOp",EDGE,"E294"),sQuery(id+"F0.wireOp",EDGE,"E295"),sQuery(id+"F0.wireOp",EDGE,"E296"),sQuery(id+"F0.wireOp",EDGE,"E297"),sQuery(id+"F0.wireOp",EDGE,"E298"),sQuery(id+"F0.wireOp",EDGE,"E299"),sQuery(id+"F0.wireOp",EDGE,"E300"),sQuery(id+"F0.wireOp",EDGE,"E301"),sQuery(id+"F0.wireOp",EDGE,"E302"),sQuery(id+"F0.wireOp",EDGE,"E303"),sQuery(id+"F0.wireOp",EDGE,"E304"),sQuery(id+"F0.wireOp",EDGE,"E305"),sQuery(id+"F0.wireOp",EDGE,"E306"),sQuery(id+"F0.wireOp",EDGE,"E307"),sQuery(id+"F0.wireOp",EDGE,"E308"),sQuery(id+"F0.wireOp",EDGE,"E309"),sQuery(id+"F0.wireOp",EDGE,"E310"),sQuery(id+"F0.wireOp",EDGE,"E311"),sQuery(id+"F0.wireOp",EDGE,"E312"),sQuery(id+"F0.wireOp",EDGE,"E313"),sQuery(id+"F0.wireOp",EDGE,"E314"),sQuery(id+"F0.wireOp",EDGE,"E315"),sQuery(id+"F0.wireOp",EDGE,"E316"),sQuery(id+"F0.wireOp",EDGE,"E317"),sQuery(id+"F0.wireOp",EDGE,"E318"),sQuery(id+"F0.wireOp",EDGE,"E319"),sQuery(id+"F0.wireOp",EDGE,"E320"),sQuery(id+"F0.wireOp",EDGE,"E321"),sQuery(id+"F0.wireOp",EDGE,"E322"),sQuery(id+"F0.wireOp",EDGE,"E323"),sQuery(id+"F0.wireOp",EDGE,"E324"),sQuery(id+"F0.wireOp",EDGE,"E325"),sQuery(id+"F0.wireOp",EDGE,"E326"),sQuery(id+"F0.wireOp",EDGE,"E327"),sQuery(id+"F0.wireOp",EDGE,"E328"),sQuery(id+"F0.wireOp",EDGE,"E329"),sQuery(id+"F0.wireOp",EDGE,"E330"),sQuery(id+"F0.wireOp",EDGE,"E331"),sQuery(id+"F0.wireOp",EDGE,"E332"),sQuery(id+"F0.wireOp",EDGE,"E333"),sQuery(id+"F0.wireOp",EDGE,"E334"),sQuery(id+"F0.wireOp",EDGE,"E335"),sQuery(id+"F0.wireOp",EDGE,"E336"),sQuery(id+"F0.wireOp",EDGE,"E337"),sQuery(id+"F0.wireOp",EDGE,"E338"),sQuery(id+"F0.wireOp",EDGE,"E339"),sQuery(id+"F0.wireOp",EDGE,"E340"),sQuery(id+"F0.wireOp",EDGE,"E341"),sQuery(id+"F0.wireOp",EDGE,"E342"),sQuery(id+"F0.wireOp",EDGE,"E343"),sQuery(id+"F0.wireOp",EDGE,"E344"),sQuery(id+"F0.wireOp",EDGE,"E345"),sQuery(id+"F0.wireOp",EDGE,"E346"),sQuery(id+"F0.wireOp",EDGE,"E347"),sQuery(id+"F0.wireOp",EDGE,"E348"),sQuery(id+"F0.wireOp",EDGE,"E349"),sQuery(id+"F0.wireOp",EDGE,"E350"),sQuery(id+"F0.wireOp",EDGE,"E351"),sQuery(id+"F0.wireOp",EDGE,"E352"),sQuery(id+"F0.wireOp",EDGE,"E353"),sQuery(id+"F0.wireOp",EDGE,"E354"),sQuery(id+"F0.wireOp",EDGE,"E355"),sQuery(id+"F0.wireOp",EDGE,"E356"),sQuery(id+"F0.wireOp",EDGE,"E357"),sQuery(id+"F0.wireOp",EDGE,"E358"),sQuery(id+"F0.wireOp",EDGE,"E359"),sQuery(id+"F0.wireOp",EDGE,"E360"),sQuery(id+"F0.wireOp",EDGE,"E361"),sQuery(id+"F0.wireOp",EDGE,"E362"),sQuery(id+"F0.wireOp",EDGE,"E363"),sQuery(id+"F0.wireOp",EDGE,"E364"),sQuery(id+"F0.wireOp",EDGE,"E365"),sQuery(id+"F0.wireOp",EDGE,"E366"),sQuery(id+"F0.wireOp",EDGE,"E367"),sQuery(id+"F0.wireOp",EDGE,"E368"),sQuery(id+"F0.wireOp",EDGE,"E369"),sQuery(id+"F0.wireOp",EDGE,"E370"),sQuery(id+"F0.wireOp",EDGE,"E371"),sQuery(id+"F0.wireOp",EDGE,"E372"),sQuery(id+"F0.wireOp",EDGE,"E373"),sQuery(id+"F0.wireOp",EDGE,"E374"),sQuery(id+"F0.wireOp",EDGE,"E375"),sQuery(id+"F0.wireOp",EDGE,"E376"),sQuery(id+"F0.wireOp",EDGE,"E377"),sQuery(id+"F0.wireOp",EDGE,"E378"),sQuery(id+"F0.wireOp",EDGE,"E379"),sQuery(id+"F0.wireOp",EDGE,"E380"),sQuery(id+"F0.wireOp",EDGE,"E381"),sQuery(id+"F0.wireOp",EDGE,"E382"),sQuery(id+"F0.wireOp",EDGE,"E383"),sQuery(id+"F0.wireOp",EDGE,"E384"),sQuery(id+"F0.wireOp",EDGE,"E385"),sQuery(id+"F0.wireOp",EDGE,"E386"),sQuery(id+"F0.wireOp",EDGE,"E387"),sQuery(id+"F0.wireOp",EDGE,"E388"),sQuery(id+"F0.wireOp",EDGE,"E389"),sQuery(id+"F0.wireOp",EDGE,"E390"),sQuery(id+"F0.wireOp",EDGE,"E391"),sQuery(id+"F0.wireOp",EDGE,"E392"),sQuery(id+"F0.wireOp",EDGE,"E393"),sQuery(id+"F0.wireOp",EDGE,"E394"),sQuery(id+"F0.wireOp",EDGE,"E395"),sQuery(id+"F0.wireOp",EDGE,"E396"),sQuery(id+"F0.wireOp",EDGE,"E397"),sQuery(id+"F0.wireOp",EDGE,"E398"),sQuery(id+"F0.wireOp",EDGE,"E399"),sQuery(id+"F0.wireOp",EDGE,"E400"),sQuery(id+"F0.wireOp",EDGE,"E401"),sQuery(id+"F0.wireOp",EDGE,"E402"),sQuery(id+"F0.wireOp",EDGE,"E403"),sQuery(id+"F0.wireOp",EDGE,"E404"),sQuery(id+"F0.wireOp",EDGE,"E405"),sQuery(id+"F0.wireOp",EDGE,"E406"),sQuery(id+"F0.wireOp",EDGE,"E407"),sQuery(id+"F0.wireOp",EDGE,"E408"),sQuery(id+"F0.wireOp",EDGE,"E409"),sQuery(id+"F0.wireOp",EDGE,"E410"),sQuery(id+"F0.wireOp",EDGE,"E411"),sQuery(id+"F0.wireOp",EDGE,"E412"),sQuery(id+"F0.wireOp",EDGE,"E413"),sQuery(id+"F0.wireOp",EDGE,"E414"),sQuery(id+"F0.wireOp",EDGE,"E415"),sQuery(id+"F0.wireOp",EDGE,"E416"),sQuery(id+"F0.wireOp",EDGE,"E417"),sQuery(id+"F0.wireOp",EDGE,"E418"),sQuery(id+"F0.wireOp",EDGE,"E419"),sQuery(id+"F0.wireOp",EDGE,"E420"),sQuery(id+"F0.wireOp",EDGE,"E421"),sQuery(id+"F0.wireOp",EDGE,"E422"),sQuery(id+"F0.wireOp",EDGE,"E423"),sQuery(id+"F0.wireOp",EDGE,"E424"),sQuery(id+"F0.wireOp",EDGE,"E425"),sQuery(id+"F0.wireOp",EDGE,"E426"),sQuery(id+"F0.wireOp",EDGE,"E427"),sQuery(id+"F0.wireOp",EDGE,"E428"),sQuery(id+"F0.wireOp",EDGE,"E429"),sQuery(id+"F0.wireOp",EDGE,"E430"),sQuery(id+"F0.wireOp",EDGE,"E431"),sQuery(id+"F0.wireOp",EDGE,"E432"),sQuery(id+"F0.wireOp",EDGE,"E433"),sQuery(id+"F0.wireOp",EDGE,"E434"),sQuery(id+"F0.wireOp",EDGE,"E435"),sQuery(id+"F0.wireOp",EDGE,"E436"),sQuery(id+"F0.wireOp",EDGE,"E437"),sQuery(id+"F0.wireOp",EDGE,"E438"),sQuery(id+"F0.wireOp",EDGE,"E439"),sQuery(id+"F0.wireOp",EDGE,"E440"),sQuery(id+"F0.wireOp",EDGE,"E441"),sQuery(id+"F0.wireOp",EDGE,"E442"),sQuery(id+"F0.wireOp",EDGE,"E443"),sQuery(id+"F0.wireOp",EDGE,"E444"),sQuery(id+"F0.wireOp",EDGE,"E445"),sQuery(id+"F0.wireOp",EDGE,"E446"),sQuery(id+"F0.wireOp",EDGE,"E447"),sQuery(id+"F0.wireOp",EDGE,"E448"),sQuery(id+"F0.wireOp",EDGE,"E449"),sQuery(id+"F0.wireOp",EDGE,"E450"),sQuery(id+"F0.wireOp",EDGE,"E451"),sQuery(id+"F0.wireOp",EDGE,"E452"),sQuery(id+"F0.wireOp",EDGE,"E453"),sQuery(id+"F0.wireOp",EDGE,"E454"),sQuery(id+"F0.wireOp",EDGE,"E455"),sQuery(id+"F0.wireOp",EDGE,"E456"),sQuery(id+"F0.wireOp",EDGE,"E457"),sQuery(id+"F0.wireOp",EDGE,"E458"),sQuery(id+"F0.wireOp",EDGE,"E459"),sQuery(id+"F0.wireOp",EDGE,"E460"),sQuery(id+"F0.wireOp",EDGE,"E461"),sQuery(id+"F0.wireOp",EDGE,"E462"),sQuery(id+"F0.wireOp",EDGE,"E463"),sQuery(id+"F0.wireOp",EDGE,"E464"),sQuery(id+"F0.wireOp",EDGE,"E465"),sQuery(id+"F0.wireOp",EDGE,"E466"),sQuery(id+"F0.wireOp",EDGE,"E467"),sQuery(id+"F0.wireOp",EDGE,"E468"),sQuery(id+"F0.wireOp",EDGE,"E469"),sQuery(id+"F0.wireOp",EDGE,"E470"),sQuery(id+"F0.wireOp",EDGE,"E471"),sQuery(id+"F0.wireOp",EDGE,"E472"),sQuery(id+"F0.wireOp",EDGE,"E473"),sQuery(id+"F0.wireOp",EDGE,"E474"),sQuery(id+"F0.wireOp",EDGE,"E475"),sQuery(id+"F0.wireOp",EDGE,"E476"),sQuery(id+"F0.wireOp",EDGE,"E477"),sQuery(id+"F0.wireOp",EDGE,"E478"),sQuery(id+"F0.wireOp",EDGE,"E479"),sQuery(id+"F0.wireOp",EDGE,"E480"),sQuery(id+"F0.wireOp",EDGE,"E481"),sQuery(id+"F0.wireOp",EDGE,"E482"),sQuery(id+"F0.wireOp",EDGE,"E483"),sQuery(id+"F0.wireOp",EDGE,"E484"),sQuery(id+"F0.wireOp",EDGE,"E485"),sQuery(id+"F0.wireOp",EDGE,"E486"),sQuery(id+"F0.wireOp",EDGE,"E487"),sQuery(id+"F0.wireOp",EDGE,"E488"),sQuery(id+"F0.wireOp",EDGE,"E489"),sQuery(id+"F0.wireOp",EDGE,"E490"),sQuery(id+"F0.wireOp",EDGE,"E491"),sQuery(id+"F0.wireOp",EDGE,"E492"),sQuery(id+"F0.wireOp",EDGE,"E493"),sQuery(id+"F0.wireOp",EDGE,"E494"),sQuery(id+"F0.wireOp",EDGE,"E495"),sQuery(id+"F0.wireOp",EDGE,"E496"),sQuery(id+"F0.wireOp",EDGE,"E497"),sQuery(id+"F0.wireOp",EDGE,"E498"),sQuery(id+"F0.wireOp",EDGE,"E499"),sQuery(id+"F0.wireOp",EDGE,"E500"),sQuery(id+"F0.wireOp",EDGE,"E501"),sQuery(id+"F0.wireOp",EDGE,"E502"),sQuery(id+"F0.wireOp",EDGE,"E503"),sQuery(id+"F0.wireOp",EDGE,"E504"),sQuery(id+"F0.wireOp",EDGE,"E505"),sQuery(id+"F0.wireOp",EDGE,"E506"),sQuery(id+"F0.wireOp",EDGE,"E507"),sQuery(id+"F0.wireOp",EDGE,"E508"),sQuery(id+"F0.wireOp",EDGE,"E509"),sQuery(id+"F0.wireOp",EDGE,"E510"),sQuery(id+"F0.wireOp",EDGE,"E511"),sQuery(id+"F0.wireOp",EDGE,"E512"),sQuery(id+"F0.wireOp",EDGE,"E513"),sQuery(id+"F0.wireOp",EDGE,"E514"),sQuery(id+"F0.wireOp",EDGE,"E515"),sQuery(id+"F0.wireOp",EDGE,"E516"),sQuery(id+"F0.wireOp",EDGE,"E517"),sQuery(id+"F0.wireOp",EDGE,"E518"),sQuery(id+"F0.wireOp",EDGE,"E519"),sQuery(id+"F0.wireOp",EDGE,"E520"),sQuery(id+"F0.wireOp",EDGE,"E521"),sQuery(id+"F0.wireOp",EDGE,"E522"),sQuery(id+"F0.wireOp",EDGE,"E523"),sQuery(id+"F0.wireOp",EDGE,"E524"),sQuery(id+"F0.wireOp",EDGE,"E525"),sQuery(id+"F0.wireOp",EDGE,"E526"),sQuery(id+"F0.wireOp",EDGE,"E527"),sQuery(id+"F0.wireOp",EDGE,"E528"),sQuery(id+"F0.wireOp",EDGE,"E529"),sQuery(id+"F0.wireOp",EDGE,"E530"),sQuery(id+"F0.wireOp",EDGE,"E531"),sQuery(id+"F0.wireOp",EDGE,"E532"),sQuery(id+"F0.wireOp",EDGE,"E533"),sQuery(id+"F0.wireOp",EDGE,"E534"),sQuery(id+"F0.wireOp",EDGE,"E535"),sQuery(id+"F0.wireOp",EDGE,"E536"),sQuery(id+"F0.wireOp",EDGE,"E537"),sQuery(id+"F0.wireOp",EDGE,"E538"),sQuery(id+"F0.wireOp",EDGE,"E539"),sQuery(id+"F0.wireOp",EDGE,"E540"),sQuery(id+"F0.wireOp",EDGE,"E541"),sQuery(id+"F0.wireOp",EDGE,"E542"),sQuery(id+"F0.wireOp",EDGE,"E543"),sQuery(id+"F0.wireOp",EDGE,"E544"),sQuery(id+"F0.wireOp",EDGE,"E545"),sQuery(id+"F0.wireOp",EDGE,"E546"),sQuery(id+"F0.wireOp",EDGE,"E547"),sQuery(id+"F0.wireOp",EDGE,"E548"),sQuery(id+"F0.wireOp",EDGE,"E549"),sQuery(id+"F0.wireOp",EDGE,"E550"),sQuery(id+"F0.wireOp",EDGE,"E551"),sQuery(id+"F0.wireOp",EDGE,"E552"),sQuery(id+"F0.wireOp",EDGE,"E553"),sQuery(id+"F0.wireOp",EDGE,"E554"),sQuery(id+"F0.wireOp",EDGE,"E555"),sQuery(id+"F0.wireOp",EDGE,"E556"),sQuery(id+"F0.wireOp",EDGE,"E557"),sQuery(id+"F0.wireOp",EDGE,"E558"),sQuery(id+"F0.wireOp",EDGE,"E559"),sQuery(id+"F0.wireOp",EDGE,"E560"),sQuery(id+"F0.wireOp",EDGE,"E561"),sQuery(id+"F0.wireOp",EDGE,"E562"),sQuery(id+"F0.wireOp",EDGE,"E563"),sQuery(id+"F0.wireOp",EDGE,"E564"),sQuery(id+"F0.wireOp",EDGE,"E565"),sQuery(id+"F0.wireOp",EDGE,"E566"),sQuery(id+"F0.wireOp",EDGE,"E567"),sQuery(id+"F0.wireOp",EDGE,"E568"),sQuery(id+"F0.wireOp",EDGE,"E569"),sQuery(id+"F0.wireOp",EDGE,"E570"),sQuery(id+"F0.wireOp",EDGE,"E571"),sQuery(id+"F0.wireOp",EDGE,"E572"),sQuery(id+"F0.wireOp",EDGE,"E573"),sQuery(id+"F0.wireOp",EDGE,"E574"),sQuery(id+"F0.wireOp",EDGE,"E575"),sQuery(id+"F0.wireOp",EDGE,"E576"),sQuery(id+"F0.wireOp",EDGE,"E577"),sQuery(id+"F0.wireOp",EDGE,"E578"),sQuery(id+"F0.wireOp",EDGE,"E579"),sQuery(id+"F0.wireOp",EDGE,"E580"),sQuery(id+"F0.wireOp",EDGE,"E581"),sQuery(id+"F0.wireOp",EDGE,"E582"),sQuery(id+"F0.wireOp",EDGE,"E583"),sQuery(id+"F0.wireOp",EDGE,"E584"),sQuery(id+"F0.wireOp",EDGE,"E585"),sQuery(id+"F0.wireOp",EDGE,"E586"),sQuery(id+"F0.wireOp",EDGE,"E587"),sQuery(id+"F0.wireOp",EDGE,"E588"),sQuery(id+"F0.wireOp",EDGE,"E589"),sQuery(id+"F0.wireOp",EDGE,"E590"),sQuery(id+"F0.wireOp",EDGE,"E591"),sQuery(id+"F0.wireOp",EDGE,"E592"),sQuery(id+"F0.wireOp",EDGE,"E593"),sQuery(id+"F0.wireOp",EDGE,"E594"),sQuery(id+"F0.wireOp",EDGE,"E595"),sQuery(id+"F0.wireOp",EDGE,"E596"),sQuery(id+"F0.wireOp",EDGE,"E597"),sQuery(id+"F0.wireOp",EDGE,"E598"),sQuery(id+"F0.wireOp",EDGE,"E599"),sQuery(id+"F0.wireOp",EDGE,"E600"),sQuery(id+"F0.wireOp",EDGE,"E601"),sQuery(id+"F0.wireOp",EDGE,"E602"),sQuery(id+"F0.wireOp",EDGE,"E603"),sQuery(id+"F0.wireOp",EDGE,"E604"),sQuery(id+"F0.wireOp",EDGE,"E605"),sQuery(id+"F0.wireOp",EDGE,"E606"),sQuery(id+"F0.wireOp",EDGE,"E607"),sQuery(id+"F0.wireOp",EDGE,"E608"),sQuery(id+"F0.wireOp",EDGE,"E609"),sQuery(id+"F0.wireOp",EDGE,"E610"),sQuery(id+"F0.wireOp",EDGE,"E611"),sQuery(id+"F0.wireOp",EDGE,"E612"),sQuery(id+"F0.wireOp",EDGE,"E613"),sQuery(id+"F0.wireOp",EDGE,"E614"),sQuery(id+"F0.wireOp",EDGE,"E615"),sQuery(id+"F0.wireOp",EDGE,"E616"),sQuery(id+"F0.wireOp",EDGE,"E617"),sQuery(id+"F0.wireOp",EDGE,"E618"),sQuery(id+"F0.wireOp",EDGE,"E619"),sQuery(id+"F0.wireOp",EDGE,"E620"),sQuery(id+"F0.wireOp",EDGE,"E621"),sQuery(id+"F0.wireOp",EDGE,"E622"),sQuery(id+"F0.wireOp",EDGE,"E623"),sQuery(id+"F0.wireOp",EDGE,"E624"),sQuery(id+"F0.wireOp",EDGE,"E625"),sQuery(id+"F0.wireOp",EDGE,"E626")])],"isStart":false});
            var sketch = newSketch(context, id + "F2", { "sketchPlane" : qUnion([Q0])});
            skCircle(sketch, "E627", {"center": v(-1.33, 0) * mm, "radius": 2.65 * mm});
            skCircle(sketch, "E628", {"center": v(-1.33, 0) * mm, "radius": 5.75 * mm});
            skSolve(sketch);
        }
        {
            var Q0;
            Q0=makeQuery(id+"F2.imprint","IMPRINT",FACE,{"disambiguationData":[TD([[makeQuery(id+"F2.imprint","IMPRINT",EDGE,{"derivedFrom":sQuery(id+"F2.wireOp",EDGE,"E627")}),-1.0]])]});
            extrude(context, id + "F3", {"entities" : qUnion([Q0]), "operationType" : NewBodyOperationType.ADD, "depth" : 1 * mm});
        }
        {
            var Q0;
            Q0=makeQuery(id+"F3.opExtrude","CAP_EDGE",EDGE,{"disambiguationData":[OSD([sQuery(id+"F2.wireOp",EDGE,"E628")])],"isStart":false});
            fillet(context, id + "F4", {"entities" : qUnion([Q0]), "radius" : 0.4 * mm, "tangentPropagation" : true, "allowEdgeOverflow" : false});
        }
    });
